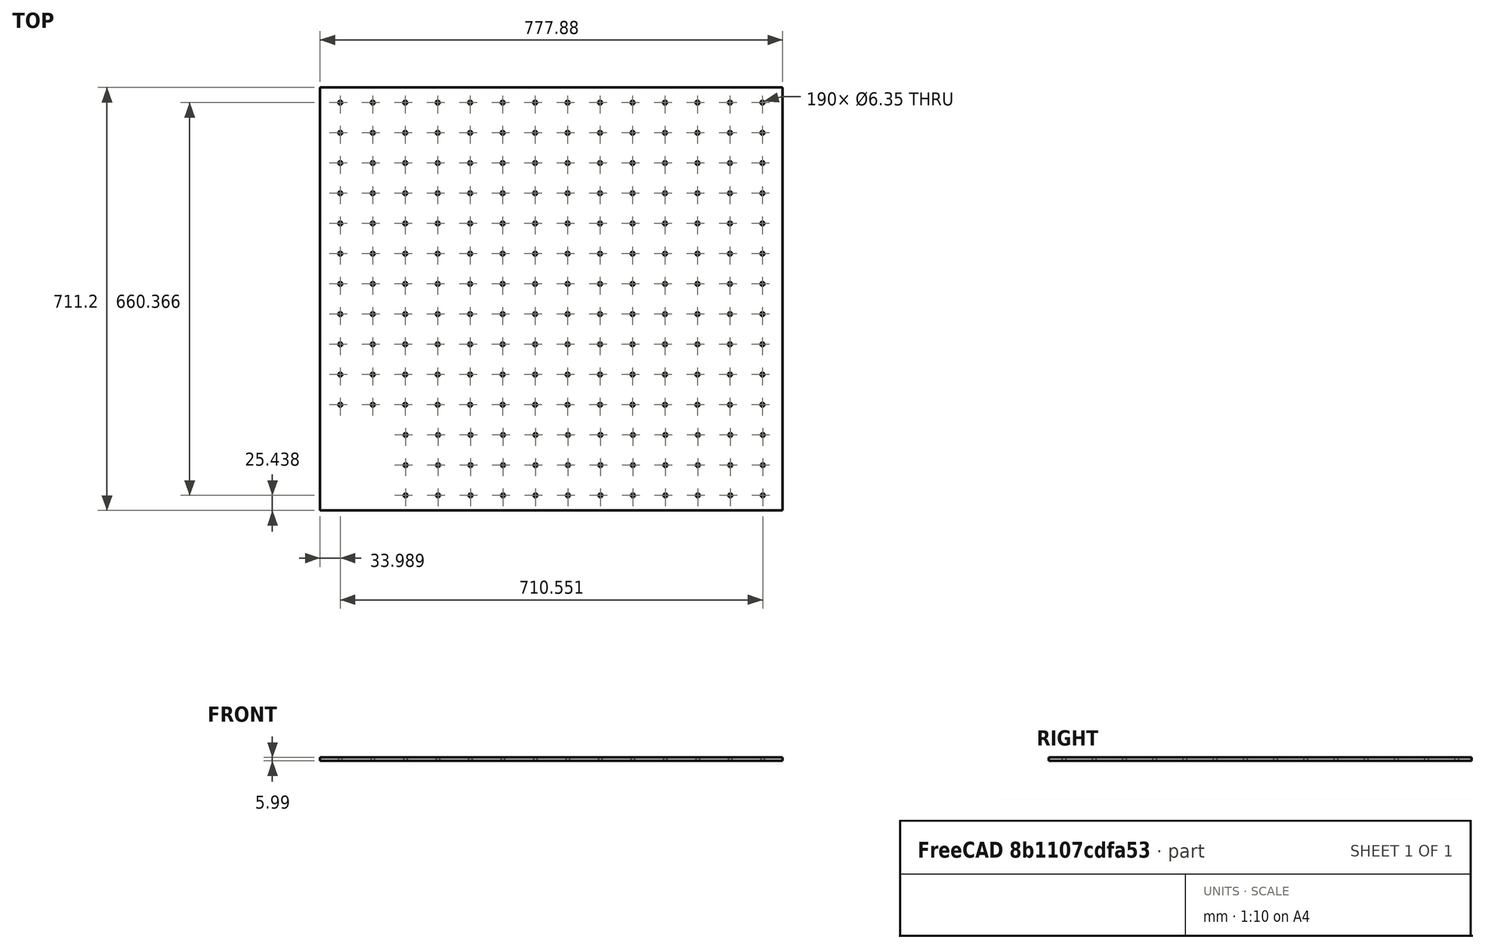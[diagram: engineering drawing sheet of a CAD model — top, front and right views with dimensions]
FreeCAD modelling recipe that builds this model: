
FCSTD DOCUMENT  (FreeCAD 0.19R24267 (Git))
Label: Inv1-P1
License: All rights reserved
LicenseURL: http://en.wikipedia.org/wiki/All_rights_reserved
objects: TechDraw::DrawViewDimension×8, TechDraw::DrawViewAnnotation×3, TechDraw::DrawProjGroupItem×2, TechDraw::DrawHatch×2, Sketcher::SketchObject×1, Part::Extrusion×1, TechDraw::DrawSVGTemplate×1, TechDraw::DrawProjGroup×1, TechDraw::DrawPage×1
note: 2 computed .brp shape members not serialized (recipe doc carries the construction recipe); baked Part::Feature solids carry a one-line shape summary decoded from their .brp

FEATURE [Sketcher::SketchObject] Sketch
  FullyConstrained = false
  sketch-geometry (389):
    g0: LineSegment StartX=-440.566 StartY=477.933 StartZ=0 EndX=337.309 EndY=477.933 EndZ=0
    g1: LineSegment StartX=337.309 StartY=477.933 StartZ=0 EndX=337.309 EndY=-233.267 EndZ=0
    g2: LineSegment StartX=337.309 StartY=-233.267 StartZ=0 EndX=-440.566 EndY=-233.267 EndZ=0
    g3: LineSegment StartX=-440.566 StartY=-233.267 StartZ=0 EndX=-440.566 EndY=477.933 EndZ=0
    g4: Circle CenterX=-406.581 CenterY=452.533 CenterZ=0 NormalX=0 NormalY=0 NormalZ=1 AngleXU=0 Radius=3.175
    g5: Circle CenterX=-351.971 CenterY=452.533 CenterZ=0 NormalX=0 NormalY=0 NormalZ=1 AngleXU=0 Radius=3.175
    g6: LineSegment StartX=-406.581 StartY=452.533 StartZ=0 EndX=-351.971 EndY=452.533 EndZ=0
    g7: Circle CenterX=-297.361 CenterY=452.533 CenterZ=0 NormalX=0 NormalY=0 NormalZ=1 AngleXU=0 Radius=3.175
    g8: LineSegment StartX=-351.971 StartY=452.533 StartZ=0 EndX=-297.361 EndY=452.533 EndZ=0
    g9: Circle CenterX=-242.751 CenterY=452.533 CenterZ=0 NormalX=0 NormalY=0 NormalZ=1 AngleXU=0 Radius=3.175
    g10: LineSegment StartX=-297.361 StartY=452.533 StartZ=0 EndX=-242.751 EndY=452.533 EndZ=0
    g11: Circle CenterX=-188.141 CenterY=452.533 CenterZ=0 NormalX=0 NormalY=0 NormalZ=1 AngleXU=0 Radius=3.175
    g12: LineSegment StartX=-242.751 StartY=452.533 StartZ=0 EndX=-188.141 EndY=452.533 EndZ=0
    g13: Circle CenterX=-133.531 CenterY=452.533 CenterZ=0 NormalX=0 NormalY=0 NormalZ=1 AngleXU=0 Radius=3.175
    g14: LineSegment StartX=-188.141 StartY=452.533 StartZ=0 EndX=-133.531 EndY=452.533 EndZ=0
    g15: Circle CenterX=-78.9213 CenterY=452.533 CenterZ=0 NormalX=0 NormalY=0 NormalZ=1 AngleXU=0 Radius=3.175
    g16: LineSegment StartX=-133.531 StartY=452.533 StartZ=0 EndX=-78.9213 EndY=452.533 EndZ=0
    g17: Circle CenterX=-24.3113 CenterY=452.533 CenterZ=0 NormalX=0 NormalY=0 NormalZ=1 AngleXU=0 Radius=3.175
    g18: LineSegment StartX=-78.9213 StartY=452.533 StartZ=0 EndX=-24.3113 EndY=452.533 EndZ=0
    g19: Circle CenterX=30.2987 CenterY=452.533 CenterZ=0 NormalX=0 NormalY=0 NormalZ=1 AngleXU=0 Radius=3.175
    g20: LineSegment StartX=-24.3113 StartY=452.533 StartZ=0 EndX=30.2987 EndY=452.533 EndZ=0
    g21: Circle CenterX=84.9087 CenterY=452.533 CenterZ=0 NormalX=0 NormalY=0 NormalZ=1 AngleXU=0 Radius=3.175
    g22: LineSegment StartX=30.2987 StartY=452.533 StartZ=0 EndX=84.9087 EndY=452.533 EndZ=0
    g23: Circle CenterX=139.519 CenterY=452.533 CenterZ=0 NormalX=0 NormalY=0 NormalZ=1 AngleXU=0 Radius=3.175
    g24: LineSegment StartX=84.9087 StartY=452.533 StartZ=0 EndX=139.519 EndY=452.533 EndZ=0
    g25: Circle CenterX=194.129 CenterY=452.533 CenterZ=0 NormalX=0 NormalY=0 NormalZ=1 AngleXU=0 Radius=3.175
    g26: LineSegment StartX=139.519 StartY=452.533 StartZ=0 EndX=194.129 EndY=452.533 EndZ=0
    g27: Circle CenterX=248.739 CenterY=452.533 CenterZ=0 NormalX=0 NormalY=0 NormalZ=1 AngleXU=0 Radius=3.175
    g28: LineSegment StartX=194.129 StartY=452.533 StartZ=0 EndX=248.739 EndY=452.533 EndZ=0
    g29: Circle CenterX=303.349 CenterY=452.533 CenterZ=0 NormalX=0 NormalY=0 NormalZ=1 AngleXU=0 Radius=3.175
    g30: LineSegment StartX=248.739 StartY=452.533 StartZ=0 EndX=303.349 EndY=452.533 EndZ=0
    g31: Circle CenterX=-406.581 CenterY=401.733 CenterZ=0 NormalX=0 NormalY=0 NormalZ=1 AngleXU=0 Radius=3.175
    g32: LineSegment StartX=-406.581 StartY=452.533 StartZ=0 EndX=-406.581 EndY=401.733 EndZ=0
    g33: Circle CenterX=-351.971 CenterY=401.733 CenterZ=0 NormalX=0 NormalY=0 NormalZ=1 AngleXU=0 Radius=3.175
    g34: LineSegment StartX=-406.581 StartY=401.733 StartZ=0 EndX=-351.971 EndY=401.733 EndZ=0
    g35: Circle CenterX=-297.361 CenterY=401.733 CenterZ=0 NormalX=0 NormalY=0 NormalZ=1 AngleXU=0 Radius=3.175
    g36: LineSegment StartX=-351.971 StartY=401.733 StartZ=0 EndX=-297.361 EndY=401.733 EndZ=0
    g37: Circle CenterX=-242.751 CenterY=401.733 CenterZ=0 NormalX=0 NormalY=0 NormalZ=1 AngleXU=0 Radius=3.175
    g38: LineSegment StartX=-297.361 StartY=401.733 StartZ=0 EndX=-242.751 EndY=401.733 EndZ=0
    g39: Circle CenterX=-188.141 CenterY=401.733 CenterZ=0 NormalX=0 NormalY=0 NormalZ=1 AngleXU=0 Radius=3.175
    g40: LineSegment StartX=-242.751 StartY=401.733 StartZ=0 EndX=-188.141 EndY=401.733 EndZ=0
    g41: Circle CenterX=-133.531 CenterY=401.733 CenterZ=0 NormalX=0 NormalY=0 NormalZ=1 AngleXU=0 Radius=3.175
    g42: LineSegment StartX=-188.141 StartY=401.733 StartZ=0 EndX=-133.531 EndY=401.733 EndZ=0
    g43: Circle CenterX=-78.9213 CenterY=401.733 CenterZ=0 NormalX=0 NormalY=0 NormalZ=1 AngleXU=0 Radius=3.175
    g44: LineSegment StartX=-133.531 StartY=401.733 StartZ=0 EndX=-78.9213 EndY=401.733 EndZ=0
    g45: Circle CenterX=-24.3113 CenterY=401.733 CenterZ=0 NormalX=0 NormalY=0 NormalZ=1 AngleXU=0 Radius=3.175
    g46: LineSegment StartX=-78.9213 StartY=401.733 StartZ=0 EndX=-24.3113 EndY=401.733 EndZ=0
    g47: Circle CenterX=30.2987 CenterY=401.733 CenterZ=0 NormalX=0 NormalY=0 NormalZ=1 AngleXU=0 Radius=3.175
    g48: LineSegment StartX=-24.3113 StartY=401.733 StartZ=0 EndX=30.2987 EndY=401.733 EndZ=0
    g49: Circle CenterX=84.9087 CenterY=401.733 CenterZ=0 NormalX=0 NormalY=0 NormalZ=1 AngleXU=0 Radius=3.175
    g50: LineSegment StartX=30.2987 StartY=401.733 StartZ=0 EndX=84.9087 EndY=401.733 EndZ=0
    g51: Circle CenterX=139.519 CenterY=401.733 CenterZ=0 NormalX=0 NormalY=0 NormalZ=1 AngleXU=0 Radius=3.175
    g52: LineSegment StartX=84.9087 StartY=401.733 StartZ=0 EndX=139.519 EndY=401.733 EndZ=0
    g53: Circle CenterX=194.129 CenterY=401.733 CenterZ=0 NormalX=0 NormalY=0 NormalZ=1 AngleXU=0 Radius=3.175
    g54: LineSegment StartX=139.519 StartY=401.733 StartZ=0 EndX=194.129 EndY=401.733 EndZ=0
    g55: Circle CenterX=248.739 CenterY=401.733 CenterZ=0 NormalX=0 NormalY=0 NormalZ=1 AngleXU=0 Radius=3.175
    g56: LineSegment StartX=194.129 StartY=401.733 StartZ=0 EndX=248.739 EndY=401.733 EndZ=0
    g57: Circle CenterX=303.349 CenterY=401.733 CenterZ=0 NormalX=0 NormalY=0 NormalZ=1 AngleXU=0 Radius=3.175
    g58: LineSegment StartX=248.739 StartY=401.733 StartZ=0 EndX=303.349 EndY=401.733 EndZ=0
    g59: Circle CenterX=-406.581 CenterY=350.933 CenterZ=0 NormalX=0 NormalY=0 NormalZ=1 AngleXU=0 Radius=3.175
    g60: LineSegment StartX=-406.581 StartY=401.733 StartZ=0 EndX=-406.581 EndY=350.933 EndZ=0
    g61: Circle CenterX=-351.971 CenterY=350.933 CenterZ=0 NormalX=0 NormalY=0 NormalZ=1 AngleXU=0 Radius=3.175
    g62: LineSegment StartX=-406.581 StartY=350.933 StartZ=0 EndX=-351.971 EndY=350.933 EndZ=0
    g63: Circle CenterX=-297.361 CenterY=350.933 CenterZ=0 NormalX=0 NormalY=0 NormalZ=1 AngleXU=0 Radius=3.175
    g64: LineSegment StartX=-351.971 StartY=350.933 StartZ=0 EndX=-297.361 EndY=350.933 EndZ=0
    g65: Circle CenterX=-242.751 CenterY=350.933 CenterZ=0 NormalX=0 NormalY=0 NormalZ=1 AngleXU=0 Radius=3.175
    g66: LineSegment StartX=-297.361 StartY=350.933 StartZ=0 EndX=-242.751 EndY=350.933 EndZ=0
    g67: Circle CenterX=-188.141 CenterY=350.933 CenterZ=0 NormalX=0 NormalY=0 NormalZ=1 AngleXU=0 Radius=3.175
    g68: LineSegment StartX=-242.751 StartY=350.933 StartZ=0 EndX=-188.141 EndY=350.933 EndZ=0
    g69: Circle CenterX=-133.531 CenterY=350.933 CenterZ=0 NormalX=0 NormalY=0 NormalZ=1 AngleXU=0 Radius=3.175
    g70: LineSegment StartX=-188.141 StartY=350.933 StartZ=0 EndX=-133.531 EndY=350.933 EndZ=0
    g71: Circle CenterX=-78.9213 CenterY=350.933 CenterZ=0 NormalX=0 NormalY=0 NormalZ=1 AngleXU=0 Radius=3.175
    g72: LineSegment StartX=-133.531 StartY=350.933 StartZ=0 EndX=-78.9213 EndY=350.933 EndZ=0
    g73: Circle CenterX=-24.3113 CenterY=350.933 CenterZ=0 NormalX=0 NormalY=0 NormalZ=1 AngleXU=0 Radius=3.175
    g74: LineSegment StartX=-78.9213 StartY=350.933 StartZ=0 EndX=-24.3113 EndY=350.933 EndZ=0
    g75: Circle CenterX=30.2987 CenterY=350.933 CenterZ=0 NormalX=0 NormalY=0 NormalZ=1 AngleXU=0 Radius=3.175
    g76: LineSegment StartX=-24.3113 StartY=350.933 StartZ=0 EndX=30.2987 EndY=350.933 EndZ=0
    g77: Circle CenterX=84.9087 CenterY=350.933 CenterZ=0 NormalX=0 NormalY=0 NormalZ=1 AngleXU=0 Radius=3.175
    g78: LineSegment StartX=30.2987 StartY=350.933 StartZ=0 EndX=84.9087 EndY=350.933 EndZ=0
    g79: Circle CenterX=139.519 CenterY=350.933 CenterZ=0 NormalX=0 NormalY=0 NormalZ=1 AngleXU=0 Radius=3.175
    g80: LineSegment StartX=84.9087 StartY=350.933 StartZ=0 EndX=139.519 EndY=350.933 EndZ=0
    g81: Circle CenterX=194.129 CenterY=350.933 CenterZ=0 NormalX=0 NormalY=0 NormalZ=1 AngleXU=0 Radius=3.175
    g82: LineSegment StartX=139.519 StartY=350.933 StartZ=0 EndX=194.129 EndY=350.933 EndZ=0
    g83: Circle CenterX=248.739 CenterY=350.933 CenterZ=0 NormalX=0 NormalY=0 NormalZ=1 AngleXU=0 Radius=3.175
    g84: LineSegment StartX=194.129 StartY=350.933 StartZ=0 EndX=248.739 EndY=350.933 EndZ=0
    g85: Circle CenterX=303.349 CenterY=350.933 CenterZ=0 NormalX=0 NormalY=0 NormalZ=1 AngleXU=0 Radius=3.175
    g86: LineSegment StartX=248.739 StartY=350.933 StartZ=0 EndX=303.349 EndY=350.933 EndZ=0
    g87: Circle CenterX=-406.581 CenterY=300.133 CenterZ=0 NormalX=0 NormalY=0 NormalZ=1 AngleXU=0 Radius=3.175
    g88: LineSegment StartX=-406.581 StartY=350.933 StartZ=0 EndX=-406.581 EndY=300.133 EndZ=0
    g89: Circle CenterX=-351.971 CenterY=300.133 CenterZ=0 NormalX=0 NormalY=0 NormalZ=1 AngleXU=0 Radius=3.175
    g90: LineSegment StartX=-406.581 StartY=300.133 StartZ=0 EndX=-351.971 EndY=300.133 EndZ=0
    g91: Circle CenterX=-297.361 CenterY=300.133 CenterZ=0 NormalX=0 NormalY=0 NormalZ=1 AngleXU=0 Radius=3.175
    g92: LineSegment StartX=-351.971 StartY=300.133 StartZ=0 EndX=-297.361 EndY=300.133 EndZ=0
    g93: Circle CenterX=-242.751 CenterY=300.133 CenterZ=0 NormalX=0 NormalY=0 NormalZ=1 AngleXU=0 Radius=3.175
    g94: LineSegment StartX=-297.361 StartY=300.133 StartZ=0 EndX=-242.751 EndY=300.133 EndZ=0
    g95: Circle CenterX=-188.141 CenterY=300.133 CenterZ=0 NormalX=0 NormalY=0 NormalZ=1 AngleXU=0 Radius=3.175
    g96: LineSegment StartX=-242.751 StartY=300.133 StartZ=0 EndX=-188.141 EndY=300.133 EndZ=0
    g97: Circle CenterX=-133.531 CenterY=300.133 CenterZ=0 NormalX=0 NormalY=0 NormalZ=1 AngleXU=0 Radius=3.175
    g98: LineSegment StartX=-188.141 StartY=300.133 StartZ=0 EndX=-133.531 EndY=300.133 EndZ=0
    g99: Circle CenterX=-78.9213 CenterY=300.133 CenterZ=0 NormalX=0 NormalY=0 NormalZ=1 AngleXU=0 Radius=3.175
    g100: LineSegment StartX=-133.531 StartY=300.133 StartZ=0 EndX=-78.9213 EndY=300.133 EndZ=0
    g101: Circle CenterX=-24.3113 CenterY=300.133 CenterZ=0 NormalX=0 NormalY=0 NormalZ=1 AngleXU=0 Radius=3.175
    g102: LineSegment StartX=-78.9213 StartY=300.133 StartZ=0 EndX=-24.3113 EndY=300.133 EndZ=0
    g103: Circle CenterX=30.2987 CenterY=300.133 CenterZ=0 NormalX=0 NormalY=0 NormalZ=1 AngleXU=0 Radius=3.175
    g104: LineSegment StartX=-24.3113 StartY=300.133 StartZ=0 EndX=30.2987 EndY=300.133 EndZ=0
    g105: Circle CenterX=84.9087 CenterY=300.133 CenterZ=0 NormalX=0 NormalY=0 NormalZ=1 AngleXU=0 Radius=3.175
    g106: LineSegment StartX=30.2987 StartY=300.133 StartZ=0 EndX=84.9087 EndY=300.133 EndZ=0
    g107: Circle CenterX=139.519 CenterY=300.133 CenterZ=0 NormalX=0 NormalY=0 NormalZ=1 AngleXU=0 Radius=3.175
    g108: LineSegment StartX=84.9087 StartY=300.133 StartZ=0 EndX=139.519 EndY=300.133 EndZ=0
    g109: Circle CenterX=194.129 CenterY=300.133 CenterZ=0 NormalX=0 NormalY=0 NormalZ=1 AngleXU=0 Radius=3.175
    g110: LineSegment StartX=139.519 StartY=300.133 StartZ=0 EndX=194.129 EndY=300.133 EndZ=0
    g111: Circle CenterX=248.739 CenterY=300.133 CenterZ=0 NormalX=0 NormalY=0 NormalZ=1 AngleXU=0 Radius=3.175
    g112: LineSegment StartX=194.129 StartY=300.133 StartZ=0 EndX=248.739 EndY=300.133 EndZ=0
    g113: Circle CenterX=303.349 CenterY=300.133 CenterZ=0 NormalX=0 NormalY=0 NormalZ=1 AngleXU=0 Radius=3.175
    g114: LineSegment StartX=248.739 StartY=300.133 StartZ=0 EndX=303.349 EndY=300.133 EndZ=0
    g115: Circle CenterX=-406.581 CenterY=249.333 CenterZ=0 NormalX=0 NormalY=0 NormalZ=1 AngleXU=0 Radius=3.175
    g116: LineSegment StartX=-406.581 StartY=300.133 StartZ=0 EndX=-406.581 EndY=249.333 EndZ=0
    g117: Circle CenterX=-351.971 CenterY=249.333 CenterZ=0 NormalX=0 NormalY=0 NormalZ=1 AngleXU=0 Radius=3.175
    g118: LineSegment StartX=-406.581 StartY=249.333 StartZ=0 EndX=-351.971 EndY=249.333 EndZ=0
    g119: Circle CenterX=-297.361 CenterY=249.333 CenterZ=0 NormalX=0 NormalY=0 NormalZ=1 AngleXU=0 Radius=3.175
    g120: LineSegment StartX=-351.971 StartY=249.333 StartZ=0 EndX=-297.361 EndY=249.333 EndZ=0
    g121: Circle CenterX=-242.751 CenterY=249.333 CenterZ=0 NormalX=0 NormalY=0 NormalZ=1 AngleXU=0 Radius=3.175
    g122: LineSegment StartX=-297.361 StartY=249.333 StartZ=0 EndX=-242.751 EndY=249.333 EndZ=0
    g123: Circle CenterX=-188.141 CenterY=249.333 CenterZ=0 NormalX=0 NormalY=0 NormalZ=1 AngleXU=0 Radius=3.175
    g124: LineSegment StartX=-242.751 StartY=249.333 StartZ=0 EndX=-188.141 EndY=249.333 EndZ=0
    g125: Circle CenterX=-133.531 CenterY=249.333 CenterZ=0 NormalX=0 NormalY=0 NormalZ=1 AngleXU=0 Radius=3.175
    g126: LineSegment StartX=-188.141 StartY=249.333 StartZ=0 EndX=-133.531 EndY=249.333 EndZ=0
    g127: Circle CenterX=-78.9213 CenterY=249.333 CenterZ=0 NormalX=0 NormalY=0 NormalZ=1 AngleXU=0 Radius=3.175
    g128: LineSegment StartX=-133.531 StartY=249.333 StartZ=0 EndX=-78.9213 EndY=249.333 EndZ=0
    g129: Circle CenterX=-24.3113 CenterY=249.333 CenterZ=0 NormalX=0 NormalY=0 NormalZ=1 AngleXU=0 Radius=3.175
    g130: LineSegment StartX=-78.9213 StartY=249.333 StartZ=0 EndX=-24.3113 EndY=249.333 EndZ=0
    g131: Circle CenterX=30.2987 CenterY=249.333 CenterZ=0 NormalX=0 NormalY=0 NormalZ=1 AngleXU=0 Radius=3.175
    g132: LineSegment StartX=-24.3113 StartY=249.333 StartZ=0 EndX=30.2987 EndY=249.333 EndZ=0
    g133: Circle CenterX=84.9087 CenterY=249.333 CenterZ=0 NormalX=0 NormalY=0 NormalZ=1 AngleXU=0 Radius=3.175
    g134: LineSegment StartX=30.2987 StartY=249.333 StartZ=0 EndX=84.9087 EndY=249.333 EndZ=0
    g135: Circle CenterX=139.519 CenterY=249.333 CenterZ=0 NormalX=0 NormalY=0 NormalZ=1 AngleXU=0 Radius=3.175
    g136: LineSegment StartX=84.9087 StartY=249.333 StartZ=0 EndX=139.519 EndY=249.333 EndZ=0
    g137: Circle CenterX=194.129 CenterY=249.333 CenterZ=0 NormalX=0 NormalY=0 NormalZ=1 AngleXU=0 Radius=3.175
    g138: LineSegment StartX=139.519 StartY=249.333 StartZ=0 EndX=194.129 EndY=249.333 EndZ=0
    g139: Circle CenterX=248.739 CenterY=249.333 CenterZ=0 NormalX=0 NormalY=0 NormalZ=1 AngleXU=0 Radius=3.175
    g140: LineSegment StartX=194.129 StartY=249.333 StartZ=0 EndX=248.739 EndY=249.333 EndZ=0
    g141: Circle CenterX=303.349 CenterY=249.333 CenterZ=0 NormalX=0 NormalY=0 NormalZ=1 AngleXU=0 Radius=3.175
    g142: LineSegment StartX=248.739 StartY=249.333 StartZ=0 EndX=303.349 EndY=249.333 EndZ=0
    g143: Circle CenterX=-406.581 CenterY=198.533 CenterZ=0 NormalX=0 NormalY=0 NormalZ=1 AngleXU=0 Radius=3.175
    g144: LineSegment StartX=-406.581 StartY=249.333 StartZ=0 EndX=-406.581 EndY=198.533 EndZ=0
    g145: Circle CenterX=-351.971 CenterY=198.533 CenterZ=0 NormalX=0 NormalY=0 NormalZ=1 AngleXU=0 Radius=3.175
    g146: LineSegment StartX=-406.581 StartY=198.533 StartZ=0 EndX=-351.971 EndY=198.533 EndZ=0
    g147: Circle CenterX=-297.361 CenterY=198.533 CenterZ=0 NormalX=0 NormalY=0 NormalZ=1 AngleXU=0 Radius=3.175
    g148: LineSegment StartX=-351.971 StartY=198.533 StartZ=0 EndX=-297.361 EndY=198.533 EndZ=0
    g149: Circle CenterX=-242.751 CenterY=198.533 CenterZ=0 NormalX=0 NormalY=0 NormalZ=1 AngleXU=0 Radius=3.175
    g150: LineSegment StartX=-297.361 StartY=198.533 StartZ=0 EndX=-242.751 EndY=198.533 EndZ=0
    g151: Circle CenterX=-188.141 CenterY=198.533 CenterZ=0 NormalX=0 NormalY=0 NormalZ=1 AngleXU=0 Radius=3.175
    g152: LineSegment StartX=-242.751 StartY=198.533 StartZ=0 EndX=-188.141 EndY=198.533 EndZ=0
    g153: Circle CenterX=-133.531 CenterY=198.533 CenterZ=0 NormalX=0 NormalY=0 NormalZ=1 AngleXU=0 Radius=3.175
    g154: LineSegment StartX=-188.141 StartY=198.533 StartZ=0 EndX=-133.531 EndY=198.533 EndZ=0
    g155: Circle CenterX=-78.9213 CenterY=198.533 CenterZ=0 NormalX=0 NormalY=0 NormalZ=1 AngleXU=0 Radius=3.175
    g156: LineSegment StartX=-133.531 StartY=198.533 StartZ=0 EndX=-78.9213 EndY=198.533 EndZ=0
    g157: Circle CenterX=-24.3113 CenterY=198.533 CenterZ=0 NormalX=0 NormalY=0 NormalZ=1 AngleXU=0 Radius=3.175
    g158: LineSegment StartX=-78.9213 StartY=198.533 StartZ=0 EndX=-24.3113 EndY=198.533 EndZ=0
    g159: Circle CenterX=30.2987 CenterY=198.533 CenterZ=0 NormalX=0 NormalY=0 NormalZ=1 AngleXU=0 Radius=3.175
    g160: LineSegment StartX=-24.3113 StartY=198.533 StartZ=0 EndX=30.2987 EndY=198.533 EndZ=0
    g161: Circle CenterX=84.9087 CenterY=198.533 CenterZ=0 NormalX=0 NormalY=0 NormalZ=1 AngleXU=0 Radius=3.175
    g162: LineSegment StartX=30.2987 StartY=198.533 StartZ=0 EndX=84.9087 EndY=198.533 EndZ=0
    g163: Circle CenterX=139.519 CenterY=198.533 CenterZ=0 NormalX=0 NormalY=0 NormalZ=1 AngleXU=0 Radius=3.175
    g164: LineSegment StartX=84.9087 StartY=198.533 StartZ=0 EndX=139.519 EndY=198.533 EndZ=0
    g165: Circle CenterX=194.129 CenterY=198.533 CenterZ=0 NormalX=0 NormalY=0 NormalZ=1 AngleXU=0 Radius=3.175
    g166: LineSegment StartX=139.519 StartY=198.533 StartZ=0 EndX=194.129 EndY=198.533 EndZ=0
    g167: Circle CenterX=248.739 CenterY=198.533 CenterZ=0 NormalX=0 NormalY=0 NormalZ=1 AngleXU=0 Radius=3.175
    g168: LineSegment StartX=194.129 StartY=198.533 StartZ=0 EndX=248.739 EndY=198.533 EndZ=0
    g169: Circle CenterX=303.349 CenterY=198.533 CenterZ=0 NormalX=0 NormalY=0 NormalZ=1 AngleXU=0 Radius=3.175
    g170: LineSegment StartX=248.739 StartY=198.533 StartZ=0 EndX=303.349 EndY=198.533 EndZ=0
    g171: Circle CenterX=-406.581 CenterY=147.733 CenterZ=0 NormalX=0 NormalY=0 NormalZ=1 AngleXU=0 Radius=3.175
    g172: LineSegment StartX=-406.581 StartY=198.533 StartZ=0 EndX=-406.581 EndY=147.733 EndZ=0
    g173: Circle CenterX=-351.971 CenterY=147.733 CenterZ=0 NormalX=0 NormalY=0 NormalZ=1 AngleXU=0 Radius=3.175
    g174: LineSegment StartX=-406.581 StartY=147.733 StartZ=0 EndX=-351.971 EndY=147.733 EndZ=0
    g175: Circle CenterX=-297.361 CenterY=147.733 CenterZ=0 NormalX=0 NormalY=0 NormalZ=1 AngleXU=0 Radius=3.175
    g176: LineSegment StartX=-351.971 StartY=147.733 StartZ=0 EndX=-297.361 EndY=147.733 EndZ=0
    g177: Circle CenterX=-242.751 CenterY=147.733 CenterZ=0 NormalX=0 NormalY=0 NormalZ=1 AngleXU=0 Radius=3.175
    g178: LineSegment StartX=-297.361 StartY=147.733 StartZ=0 EndX=-242.751 EndY=147.733 EndZ=0
    g179: Circle CenterX=-188.141 CenterY=147.733 CenterZ=0 NormalX=0 NormalY=0 NormalZ=1 AngleXU=0 Radius=3.175
    g180: LineSegment StartX=-242.751 StartY=147.733 StartZ=0 EndX=-188.141 EndY=147.733 EndZ=0
    g181: Circle CenterX=-133.531 CenterY=147.733 CenterZ=0 NormalX=0 NormalY=0 NormalZ=1 AngleXU=0 Radius=3.175
    g182: LineSegment StartX=-188.141 StartY=147.733 StartZ=0 EndX=-133.531 EndY=147.733 EndZ=0
    g183: Circle CenterX=-78.9213 CenterY=147.733 CenterZ=0 NormalX=0 NormalY=0 NormalZ=1 AngleXU=0 Radius=3.175
    g184: LineSegment StartX=-133.531 StartY=147.733 StartZ=0 EndX=-78.9213 EndY=147.733 EndZ=0
    g185: Circle CenterX=-24.3113 CenterY=147.733 CenterZ=0 NormalX=0 NormalY=0 NormalZ=1 AngleXU=0 Radius=3.175
    g186: LineSegment StartX=-78.9213 StartY=147.733 StartZ=0 EndX=-24.3113 EndY=147.733 EndZ=0
    g187: Circle CenterX=30.2987 CenterY=147.733 CenterZ=0 NormalX=0 NormalY=0 NormalZ=1 AngleXU=0 Radius=3.175
    g188: LineSegment StartX=-24.3113 StartY=147.733 StartZ=0 EndX=30.2987 EndY=147.733 EndZ=0
    g189: Circle CenterX=84.9087 CenterY=147.733 CenterZ=0 NormalX=0 NormalY=0 NormalZ=1 AngleXU=0 Radius=3.175
    g190: LineSegment StartX=30.2987 StartY=147.733 StartZ=0 EndX=84.9087 EndY=147.733 EndZ=0
    g191: Circle CenterX=139.519 CenterY=147.733 CenterZ=0 NormalX=0 NormalY=0 NormalZ=1 AngleXU=0 Radius=3.175
    g192: LineSegment StartX=84.9087 StartY=147.733 StartZ=0 EndX=139.519 EndY=147.733 EndZ=0
    g193: Circle CenterX=194.129 CenterY=147.733 CenterZ=0 NormalX=0 NormalY=0 NormalZ=1 AngleXU=0 Radius=3.175
    g194: LineSegment StartX=139.519 StartY=147.733 StartZ=0 EndX=194.129 EndY=147.733 EndZ=0
    g195: Circle CenterX=248.739 CenterY=147.733 CenterZ=0 NormalX=0 NormalY=0 NormalZ=1 AngleXU=0 Radius=3.175
    g196: LineSegment StartX=194.129 StartY=147.733 StartZ=0 EndX=248.739 EndY=147.733 EndZ=0
    g197: Circle CenterX=303.349 CenterY=147.733 CenterZ=0 NormalX=0 NormalY=0 NormalZ=1 AngleXU=0 Radius=3.175
    g198: LineSegment StartX=248.739 StartY=147.733 StartZ=0 EndX=303.349 EndY=147.733 EndZ=0
    g199: Circle CenterX=-406.581 CenterY=96.9335 CenterZ=0 NormalX=0 NormalY=0 NormalZ=1 AngleXU=0 Radius=3.175
    g200: LineSegment StartX=-406.581 StartY=147.733 StartZ=0 EndX=-406.581 EndY=96.9335 EndZ=0
    g201: Circle CenterX=-351.971 CenterY=96.9335 CenterZ=0 NormalX=0 NormalY=0 NormalZ=1 AngleXU=0 Radius=3.175
    g202: LineSegment StartX=-406.581 StartY=96.9335 StartZ=0 EndX=-351.971 EndY=96.9335 EndZ=0
    g203: Circle CenterX=-297.361 CenterY=96.9335 CenterZ=0 NormalX=0 NormalY=0 NormalZ=1 AngleXU=0 Radius=3.175
    g204: LineSegment StartX=-351.971 StartY=96.9335 StartZ=0 EndX=-297.361 EndY=96.9335 EndZ=0
    g205: Circle CenterX=-242.751 CenterY=96.9335 CenterZ=0 NormalX=0 NormalY=0 NormalZ=1 AngleXU=0 Radius=3.175
    g206: LineSegment StartX=-297.361 StartY=96.9335 StartZ=0 EndX=-242.751 EndY=96.9335 EndZ=0
    g207: Circle CenterX=-188.141 CenterY=96.9335 CenterZ=0 NormalX=0 NormalY=0 NormalZ=1 AngleXU=0 Radius=3.175
    g208: LineSegment StartX=-242.751 StartY=96.9335 StartZ=0 EndX=-188.141 EndY=96.9335 EndZ=0
    g209: Circle CenterX=-133.531 CenterY=96.9335 CenterZ=0 NormalX=0 NormalY=0 NormalZ=1 AngleXU=0 Radius=3.175
    g210: LineSegment StartX=-188.141 StartY=96.9335 StartZ=0 EndX=-133.531 EndY=96.9335 EndZ=0
    g211: Circle CenterX=-78.9213 CenterY=96.9335 CenterZ=0 NormalX=0 NormalY=0 NormalZ=1 AngleXU=0 Radius=3.175
    g212: LineSegment StartX=-133.531 StartY=96.9335 StartZ=0 EndX=-78.9213 EndY=96.9335 EndZ=0
    g213: Circle CenterX=-24.3113 CenterY=96.9335 CenterZ=0 NormalX=0 NormalY=0 NormalZ=1 AngleXU=0 Radius=3.175
    g214: LineSegment StartX=-78.9213 StartY=96.9335 StartZ=0 EndX=-24.3113 EndY=96.9335 EndZ=0
    g215: Circle CenterX=30.2987 CenterY=96.9335 CenterZ=0 NormalX=0 NormalY=0 NormalZ=1 AngleXU=0 Radius=3.175
    g216: LineSegment StartX=-24.3113 StartY=96.9335 StartZ=0 EndX=30.2987 EndY=96.9335 EndZ=0
    g217: Circle CenterX=84.9087 CenterY=96.9335 CenterZ=0 NormalX=0 NormalY=0 NormalZ=1 AngleXU=0 Radius=3.175
    g218: LineSegment StartX=30.2987 StartY=96.9335 StartZ=0 EndX=84.9087 EndY=96.9335 EndZ=0
    g219: Circle CenterX=139.519 CenterY=96.9335 CenterZ=0 NormalX=0 NormalY=0 NormalZ=1 AngleXU=0 Radius=3.175
    g220: LineSegment StartX=84.9087 StartY=96.9335 StartZ=0 EndX=139.519 EndY=96.9335 EndZ=0
    g221: Circle CenterX=194.129 CenterY=96.9335 CenterZ=0 NormalX=0 NormalY=0 NormalZ=1 AngleXU=0 Radius=3.175
    g222: LineSegment StartX=139.519 StartY=96.9335 StartZ=0 EndX=194.129 EndY=96.9335 EndZ=0
    g223: Circle CenterX=248.739 CenterY=96.9335 CenterZ=0 NormalX=0 NormalY=0 NormalZ=1 AngleXU=0 Radius=3.175
    g224: LineSegment StartX=194.129 StartY=96.9335 StartZ=0 EndX=248.739 EndY=96.9335 EndZ=0
    g225: Circle CenterX=303.349 CenterY=96.9335 CenterZ=0 NormalX=0 NormalY=0 NormalZ=1 AngleXU=0 Radius=3.175
    g226: LineSegment StartX=248.739 StartY=96.9335 StartZ=0 EndX=303.349 EndY=96.9335 EndZ=0
    g227: Circle CenterX=-406.581 CenterY=46.1335 CenterZ=0 NormalX=0 NormalY=0 NormalZ=1 AngleXU=0 Radius=3.175
    g228: LineSegment StartX=-406.581 StartY=96.9335 StartZ=0 EndX=-406.581 EndY=46.1335 EndZ=0
    g229: Circle CenterX=-351.971 CenterY=46.1335 CenterZ=0 NormalX=0 NormalY=0 NormalZ=1 AngleXU=0 Radius=3.175
    g230: LineSegment StartX=-406.581 StartY=46.1335 StartZ=0 EndX=-351.971 EndY=46.1335 EndZ=0
    g231: Circle CenterX=-297.361 CenterY=46.1335 CenterZ=0 NormalX=0 NormalY=0 NormalZ=1 AngleXU=0 Radius=3.175
    g232: LineSegment StartX=-351.971 StartY=46.1335 StartZ=0 EndX=-297.361 EndY=46.1335 EndZ=0
    g233: Circle CenterX=-242.751 CenterY=46.1335 CenterZ=0 NormalX=0 NormalY=0 NormalZ=1 AngleXU=0 Radius=3.175
    g234: LineSegment StartX=-297.361 StartY=46.1335 StartZ=0 EndX=-242.751 EndY=46.1335 EndZ=0
    g235: Circle CenterX=-188.141 CenterY=46.1335 CenterZ=0 NormalX=0 NormalY=0 NormalZ=1 AngleXU=0 Radius=3.175
    g236: LineSegment StartX=-242.751 StartY=46.1335 StartZ=0 EndX=-188.141 EndY=46.1335 EndZ=0
    g237: Circle CenterX=-133.531 CenterY=46.1335 CenterZ=0 NormalX=0 NormalY=0 NormalZ=1 AngleXU=0 Radius=3.175
    g238: LineSegment StartX=-188.141 StartY=46.1335 StartZ=0 EndX=-133.531 EndY=46.1335 EndZ=0
    g239: Circle CenterX=-78.9213 CenterY=46.1335 CenterZ=0 NormalX=0 NormalY=0 NormalZ=1 AngleXU=0 Radius=3.175
    g240: LineSegment StartX=-133.531 StartY=46.1335 StartZ=0 EndX=-78.9213 EndY=46.1335 EndZ=0
    g241: Circle CenterX=-24.3113 CenterY=46.1335 CenterZ=0 NormalX=0 NormalY=0 NormalZ=1 AngleXU=0 Radius=3.175
    g242: LineSegment StartX=-78.9213 StartY=46.1335 StartZ=0 EndX=-24.3113 EndY=46.1335 EndZ=0
    g243: Circle CenterX=30.2987 CenterY=46.1335 CenterZ=0 NormalX=0 NormalY=0 NormalZ=1 AngleXU=0 Radius=3.175
    g244: LineSegment StartX=-24.3113 StartY=46.1335 StartZ=0 EndX=30.2987 EndY=46.1335 EndZ=0
    g245: Circle CenterX=84.9087 CenterY=46.1335 CenterZ=0 NormalX=0 NormalY=0 NormalZ=1 AngleXU=0 Radius=3.175
    g246: LineSegment StartX=30.2987 StartY=46.1335 StartZ=0 EndX=84.9087 EndY=46.1335 EndZ=0
    g247: Circle CenterX=139.519 CenterY=46.1335 CenterZ=0 NormalX=0 NormalY=0 NormalZ=1 AngleXU=0 Radius=3.175
    g248: LineSegment StartX=84.9087 StartY=46.1335 StartZ=0 EndX=139.519 EndY=46.1335 EndZ=0
    g249: Circle CenterX=194.129 CenterY=46.1335 CenterZ=0 NormalX=0 NormalY=0 NormalZ=1 AngleXU=0 Radius=3.175
    g250: LineSegment StartX=139.519 StartY=46.1335 StartZ=0 EndX=194.129 EndY=46.1335 EndZ=0
    g251: Circle CenterX=248.739 CenterY=46.1335 CenterZ=0 NormalX=0 NormalY=0 NormalZ=1 AngleXU=0 Radius=3.175
    g252: LineSegment StartX=194.129 StartY=46.1335 StartZ=0 EndX=248.739 EndY=46.1335 EndZ=0
    g253: Circle CenterX=303.349 CenterY=46.1335 CenterZ=0 NormalX=0 NormalY=0 NormalZ=1 AngleXU=0 Radius=3.175
    g254: LineSegment StartX=248.739 StartY=46.1335 StartZ=0 EndX=303.349 EndY=46.1335 EndZ=0
    g255: Circle CenterX=-406.581 CenterY=-4.66652 CenterZ=0 NormalX=0 NormalY=0 NormalZ=1 AngleXU=0 Radius=3.175
    g256: LineSegment StartX=-406.581 StartY=46.1335 StartZ=0 EndX=-406.581 EndY=-4.66652 EndZ=0
    g257: Circle CenterX=-351.971 CenterY=-4.66652 CenterZ=0 NormalX=0 NormalY=0 NormalZ=1 AngleXU=0 Radius=3.175
    g258: LineSegment StartX=-406.581 StartY=-4.66652 StartZ=0 EndX=-351.971 EndY=-4.66652 EndZ=0
    g259: Circle CenterX=-297.361 CenterY=-4.66652 CenterZ=0 NormalX=0 NormalY=0 NormalZ=1 AngleXU=0 Radius=3.175
    g260: LineSegment StartX=-351.971 StartY=-4.66652 StartZ=0 EndX=-297.361 EndY=-4.66652 EndZ=0
    g261: Circle CenterX=-242.751 CenterY=-4.66652 CenterZ=0 NormalX=0 NormalY=0 NormalZ=1 AngleXU=0 Radius=3.175
    g262: LineSegment StartX=-297.361 StartY=-4.66652 StartZ=0 EndX=-242.751 EndY=-4.66652 EndZ=0
    g263: Circle CenterX=-188.141 CenterY=-4.66652 CenterZ=0 NormalX=0 NormalY=0 NormalZ=1 AngleXU=0 Radius=3.175
    g264: LineSegment StartX=-242.751 StartY=-4.66652 StartZ=0 EndX=-188.141 EndY=-4.66652 EndZ=0
    g265: Circle CenterX=-133.531 CenterY=-4.66652 CenterZ=0 NormalX=0 NormalY=0 NormalZ=1 AngleXU=0 Radius=3.175
    g266: LineSegment StartX=-188.141 StartY=-4.66652 StartZ=0 EndX=-133.531 EndY=-4.66652 EndZ=0
    g267: Circle CenterX=-78.9213 CenterY=-4.66652 CenterZ=0 NormalX=0 NormalY=0 NormalZ=1 AngleXU=0 Radius=3.175
    g268: LineSegment StartX=-133.531 StartY=-4.66652 StartZ=0 EndX=-78.9213 EndY=-4.66652 EndZ=0
    g269: Circle CenterX=-24.3113 CenterY=-4.66652 CenterZ=0 NormalX=0 NormalY=0 NormalZ=1 AngleXU=0 Radius=3.175
    g270: LineSegment StartX=-78.9213 StartY=-4.66652 StartZ=0 EndX=-24.3113 EndY=-4.66652 EndZ=0
    g271: Circle CenterX=30.2987 CenterY=-4.66652 CenterZ=0 NormalX=0 NormalY=0 NormalZ=1 AngleXU=0 Radius=3.175
    g272: LineSegment StartX=-24.3113 StartY=-4.66652 StartZ=0 EndX=30.2987 EndY=-4.66652 EndZ=0
    g273: Circle CenterX=84.9087 CenterY=-4.66652 CenterZ=0 NormalX=0 NormalY=0 NormalZ=1 AngleXU=0 Radius=3.175
    g274: LineSegment StartX=30.2987 StartY=-4.66652 StartZ=0 EndX=84.9087 EndY=-4.66652 EndZ=0
    g275: Circle CenterX=139.519 CenterY=-4.66652 CenterZ=0 NormalX=0 NormalY=0 NormalZ=1 AngleXU=0 Radius=3.175
    g276: LineSegment StartX=84.9087 StartY=-4.66652 StartZ=0 EndX=139.519 EndY=-4.66652 EndZ=0
    g277: Circle CenterX=194.129 CenterY=-4.66652 CenterZ=0 NormalX=0 NormalY=0 NormalZ=1 AngleXU=0 Radius=3.175
    g278: LineSegment StartX=139.519 StartY=-4.66652 StartZ=0 EndX=194.129 EndY=-4.66652 EndZ=0
    g279: Circle CenterX=248.739 CenterY=-4.66652 CenterZ=0 NormalX=0 NormalY=0 NormalZ=1 AngleXU=0 Radius=3.175
    g280: LineSegment StartX=194.129 StartY=-4.66652 StartZ=0 EndX=248.739 EndY=-4.66652 EndZ=0
    g281: Circle CenterX=303.349 CenterY=-4.66652 CenterZ=0 NormalX=0 NormalY=0 NormalZ=1 AngleXU=0 Radius=3.175
    g282: LineSegment StartX=248.739 StartY=-4.66652 StartZ=0 EndX=303.349 EndY=-4.66652 EndZ=0
    g283: Circle CenterX=-406.581 CenterY=-55.4665 CenterZ=0 NormalX=0 NormalY=0 NormalZ=1 AngleXU=0 Radius=3.175
    g284: LineSegment StartX=-406.581 StartY=-4.66652 StartZ=0 EndX=-406.581 EndY=-55.4665 EndZ=0
    g285: Circle CenterX=-351.971 CenterY=-55.4665 CenterZ=0 NormalX=0 NormalY=0 NormalZ=1 AngleXU=0 Radius=3.175
    g286: LineSegment StartX=-406.581 StartY=-55.4665 StartZ=0 EndX=-351.971 EndY=-55.4665 EndZ=0
    g287: Circle CenterX=-297.361 CenterY=-55.4665 CenterZ=0 NormalX=0 NormalY=0 NormalZ=1 AngleXU=0 Radius=3.175
    g288: LineSegment StartX=-351.971 StartY=-55.4665 StartZ=0 EndX=-297.361 EndY=-55.4665 EndZ=0
    g289: Circle CenterX=-242.751 CenterY=-55.4665 CenterZ=0 NormalX=0 NormalY=0 NormalZ=1 AngleXU=0 Radius=3.175
    g290: LineSegment StartX=-297.361 StartY=-55.4665 StartZ=0 EndX=-242.751 EndY=-55.4665 EndZ=0
    g291: Circle CenterX=-188.141 CenterY=-55.4665 CenterZ=0 NormalX=0 NormalY=0 NormalZ=1 AngleXU=0 Radius=3.175
    g292: LineSegment StartX=-242.751 StartY=-55.4665 StartZ=0 EndX=-188.141 EndY=-55.4665 EndZ=0
    g293: Circle CenterX=-133.531 CenterY=-55.4665 CenterZ=0 NormalX=0 NormalY=0 NormalZ=1 AngleXU=0 Radius=3.175
    g294: LineSegment StartX=-188.141 StartY=-55.4665 StartZ=0 EndX=-133.531 EndY=-55.4665 EndZ=0
    g295: Circle CenterX=-78.9213 CenterY=-55.4665 CenterZ=0 NormalX=0 NormalY=0 NormalZ=1 AngleXU=0 Radius=3.175
    g296: LineSegment StartX=-133.531 StartY=-55.4665 StartZ=0 EndX=-78.9213 EndY=-55.4665 EndZ=0
    g297: Circle CenterX=-24.3113 CenterY=-55.4665 CenterZ=0 NormalX=0 NormalY=0 NormalZ=1 AngleXU=0 Radius=3.175
    g298: LineSegment StartX=-78.9213 StartY=-55.4665 StartZ=0 EndX=-24.3113 EndY=-55.4665 EndZ=0
    g299: Circle CenterX=30.2987 CenterY=-55.4665 CenterZ=0 NormalX=0 NormalY=0 NormalZ=1 AngleXU=0 Radius=3.175
    g300: LineSegment StartX=-24.3113 StartY=-55.4665 StartZ=0 EndX=30.2987 EndY=-55.4665 EndZ=0
    g301: Circle CenterX=84.9087 CenterY=-55.4665 CenterZ=0 NormalX=0 NormalY=0 NormalZ=1 AngleXU=0 Radius=3.175
    g302: LineSegment StartX=30.2987 StartY=-55.4665 StartZ=0 EndX=84.9087 EndY=-55.4665 EndZ=0
    g303: Circle CenterX=139.519 CenterY=-55.4665 CenterZ=0 NormalX=0 NormalY=0 NormalZ=1 AngleXU=0 Radius=3.175
    g304: LineSegment StartX=84.9087 StartY=-55.4665 StartZ=0 EndX=139.519 EndY=-55.4665 EndZ=0
    g305: Circle CenterX=194.129 CenterY=-55.4665 CenterZ=0 NormalX=0 NormalY=0 NormalZ=1 AngleXU=0 Radius=3.175
    g306: LineSegment StartX=139.519 StartY=-55.4665 StartZ=0 EndX=194.129 EndY=-55.4665 EndZ=0
    g307: Circle CenterX=248.739 CenterY=-55.4665 CenterZ=0 NormalX=0 NormalY=0 NormalZ=1 AngleXU=0 Radius=3.175
    g308: LineSegment StartX=194.129 StartY=-55.4665 StartZ=0 EndX=248.739 EndY=-55.4665 EndZ=0
    g309: Circle CenterX=303.349 CenterY=-55.4665 CenterZ=0 NormalX=0 NormalY=0 NormalZ=1 AngleXU=0 Radius=3.175
    g310: LineSegment StartX=248.739 StartY=-55.4665 StartZ=0 EndX=303.349 EndY=-55.4665 EndZ=0
    g311: LineSegment StartX=-406.581 StartY=-55.4665 StartZ=0 EndX=-406.581 EndY=-106.267 EndZ=0
    g312: LineSegment StartX=-405.96 StartY=-106.232 StartZ=0 EndX=-351.35 EndY=-106.232 EndZ=0
    g313: Circle CenterX=-296.741 CenterY=-106.232 CenterZ=0 NormalX=0 NormalY=0 NormalZ=1 AngleXU=0 Radius=3.175
    g314: LineSegment StartX=-351.351 StartY=-106.232 StartZ=0 EndX=-296.741 EndY=-106.232 EndZ=0
    g315: Circle CenterX=-242.131 CenterY=-106.232 CenterZ=0 NormalX=0 NormalY=0 NormalZ=1 AngleXU=0 Radius=3.175
    g316: LineSegment StartX=-296.741 StartY=-106.232 StartZ=0 EndX=-242.131 EndY=-106.232 EndZ=0
    g317: Circle CenterX=-187.521 CenterY=-106.232 CenterZ=0 NormalX=0 NormalY=0 NormalZ=1 AngleXU=0 Radius=3.175
    g318: LineSegment StartX=-242.131 StartY=-106.232 StartZ=0 EndX=-187.521 EndY=-106.232 EndZ=0
    g319: Circle CenterX=-132.911 CenterY=-106.232 CenterZ=0 NormalX=0 NormalY=0 NormalZ=1 AngleXU=0 Radius=3.175
    g320: LineSegment StartX=-187.521 StartY=-106.232 StartZ=0 EndX=-132.911 EndY=-106.232 EndZ=0
    g321: Circle CenterX=-78.3007 CenterY=-106.232 CenterZ=0 NormalX=0 NormalY=0 NormalZ=1 AngleXU=0 Radius=3.175
    g322: LineSegment StartX=-132.911 StartY=-106.232 StartZ=0 EndX=-78.3007 EndY=-106.232 EndZ=0
    g323: Circle CenterX=-23.6907 CenterY=-106.232 CenterZ=0 NormalX=0 NormalY=0 NormalZ=1 AngleXU=0 Radius=3.175
    g324: LineSegment StartX=-78.3007 StartY=-106.232 StartZ=0 EndX=-23.6907 EndY=-106.232 EndZ=0
    g325: Circle CenterX=30.9193 CenterY=-106.232 CenterZ=0 NormalX=0 NormalY=0 NormalZ=1 AngleXU=0 Radius=3.175
    g326: LineSegment StartX=-23.6907 StartY=-106.232 StartZ=0 EndX=30.9193 EndY=-106.232 EndZ=0
    g327: Circle CenterX=85.5293 CenterY=-106.232 CenterZ=0 NormalX=0 NormalY=0 NormalZ=1 AngleXU=0 Radius=3.175
    g328: LineSegment StartX=30.9193 StartY=-106.232 StartZ=0 EndX=85.5293 EndY=-106.232 EndZ=0
    g329: Circle CenterX=140.139 CenterY=-106.232 CenterZ=0 NormalX=0 NormalY=0 NormalZ=1 AngleXU=0 Radius=3.175
    g330: LineSegment StartX=85.5293 StartY=-106.232 StartZ=0 EndX=140.139 EndY=-106.232 EndZ=0
    g331: Circle CenterX=194.749 CenterY=-106.232 CenterZ=0 NormalX=0 NormalY=0 NormalZ=1 AngleXU=0 Radius=3.175
    g332: LineSegment StartX=140.139 StartY=-106.232 StartZ=0 EndX=194.749 EndY=-106.232 EndZ=0
    g333: Circle CenterX=249.359 CenterY=-106.232 CenterZ=0 NormalX=0 NormalY=0 NormalZ=1 AngleXU=0 Radius=3.175
    g334: LineSegment StartX=194.749 StartY=-106.232 StartZ=0 EndX=249.359 EndY=-106.232 EndZ=0
    g335: Circle CenterX=303.969 CenterY=-106.232 CenterZ=0 NormalX=0 NormalY=0 NormalZ=1 AngleXU=0 Radius=3.175
    g336: LineSegment StartX=249.359 StartY=-106.232 StartZ=0 EndX=303.969 EndY=-106.232 EndZ=0
    g337: LineSegment StartX=-405.961 StartY=-106.232 StartZ=0 EndX=-405.961 EndY=-157.032 EndZ=0
    g338: LineSegment StartX=-405.961 StartY=-157.032 StartZ=0 EndX=-351.351 EndY=-157.032 EndZ=0
    g339: Circle CenterX=-296.74 CenterY=-157.032 CenterZ=0 NormalX=0 NormalY=0 NormalZ=1 AngleXU=0 Radius=3.175
    g340: LineSegment StartX=-351.35 StartY=-157.032 StartZ=0 EndX=-296.74 EndY=-157.032 EndZ=0
    g341: Circle CenterX=-242.13 CenterY=-157.032 CenterZ=0 NormalX=0 NormalY=0 NormalZ=1 AngleXU=0 Radius=3.175
    g342: LineSegment StartX=-296.74 StartY=-157.032 StartZ=0 EndX=-242.13 EndY=-157.032 EndZ=0
    g343: Circle CenterX=-187.52 CenterY=-157.032 CenterZ=0 NormalX=0 NormalY=0 NormalZ=1 AngleXU=0 Radius=3.175
    g344: LineSegment StartX=-242.13 StartY=-157.032 StartZ=0 EndX=-187.52 EndY=-157.032 EndZ=0
    g345: Circle CenterX=-132.91 CenterY=-157.032 CenterZ=0 NormalX=0 NormalY=0 NormalZ=1 AngleXU=0 Radius=3.175
    g346: LineSegment StartX=-187.52 StartY=-157.032 StartZ=0 EndX=-132.91 EndY=-157.032 EndZ=0
    g347: Circle CenterX=-78.3004 CenterY=-157.032 CenterZ=0 NormalX=0 NormalY=0 NormalZ=1 AngleXU=0 Radius=3.175
    g348: LineSegment StartX=-132.91 StartY=-157.032 StartZ=0 EndX=-78.3004 EndY=-157.032 EndZ=0
    g349: Circle CenterX=-23.6904 CenterY=-157.032 CenterZ=0 NormalX=0 NormalY=0 NormalZ=1 AngleXU=0 Radius=3.175
    g350: LineSegment StartX=-78.3004 StartY=-157.032 StartZ=0 EndX=-23.6904 EndY=-157.032 EndZ=0
    g351: Circle CenterX=30.9196 CenterY=-157.032 CenterZ=0 NormalX=0 NormalY=0 NormalZ=1 AngleXU=0 Radius=3.175
    g352: LineSegment StartX=-23.6904 StartY=-157.032 StartZ=0 EndX=30.9196 EndY=-157.032 EndZ=0
    g353: Circle CenterX=85.5296 CenterY=-157.032 CenterZ=0 NormalX=0 NormalY=0 NormalZ=1 AngleXU=0 Radius=3.175
    g354: LineSegment StartX=30.9196 StartY=-157.032 StartZ=0 EndX=85.5296 EndY=-157.032 EndZ=0
    g355: Circle CenterX=140.14 CenterY=-157.032 CenterZ=0 NormalX=0 NormalY=0 NormalZ=1 AngleXU=0 Radius=3.175
    g356: LineSegment StartX=85.5296 StartY=-157.032 StartZ=0 EndX=140.14 EndY=-157.032 EndZ=0
    g357: Circle CenterX=194.75 CenterY=-157.032 CenterZ=0 NormalX=0 NormalY=0 NormalZ=1 AngleXU=0 Radius=3.175
    g358: LineSegment StartX=140.14 StartY=-157.032 StartZ=0 EndX=194.75 EndY=-157.032 EndZ=0
    g359: Circle CenterX=249.36 CenterY=-157.032 CenterZ=0 NormalX=0 NormalY=0 NormalZ=1 AngleXU=0 Radius=3.175
    g360: LineSegment StartX=194.75 StartY=-157.032 StartZ=0 EndX=249.36 EndY=-157.032 EndZ=0
    g361: Circle CenterX=303.97 CenterY=-157.032 CenterZ=0 NormalX=0 NormalY=0 NormalZ=1 AngleXU=0 Radius=3.175
    g362: LineSegment StartX=249.36 StartY=-157.032 StartZ=0 EndX=303.97 EndY=-157.032 EndZ=0
    g363: LineSegment StartX=-405.961 StartY=-157.032 StartZ=0 EndX=-405.961 EndY=-207.832 EndZ=0
    g364: LineSegment StartX=-405.96 StartY=-207.832 StartZ=0 EndX=-351.35 EndY=-207.832 EndZ=0
    g365: Circle CenterX=-296.74 CenterY=-207.832 CenterZ=0 NormalX=0 NormalY=0 NormalZ=1 AngleXU=0 Radius=3.175
    g366: LineSegment StartX=-351.35 StartY=-207.832 StartZ=0 EndX=-296.74 EndY=-207.832 EndZ=0
    g367: Circle CenterX=-242.13 CenterY=-207.832 CenterZ=0 NormalX=0 NormalY=0 NormalZ=1 AngleXU=0 Radius=3.175
    g368: LineSegment StartX=-296.74 StartY=-207.832 StartZ=0 EndX=-242.13 EndY=-207.832 EndZ=0
    g369: Circle CenterX=-187.52 CenterY=-207.832 CenterZ=0 NormalX=0 NormalY=0 NormalZ=1 AngleXU=0 Radius=3.175
    g370: LineSegment StartX=-242.13 StartY=-207.832 StartZ=0 EndX=-187.52 EndY=-207.832 EndZ=0
    g371: Circle CenterX=-132.91 CenterY=-207.832 CenterZ=0 NormalX=0 NormalY=0 NormalZ=1 AngleXU=0 Radius=3.175
    g372: LineSegment StartX=-187.52 StartY=-207.832 StartZ=0 EndX=-132.91 EndY=-207.832 EndZ=0
    g373: Circle CenterX=-78.3004 CenterY=-207.832 CenterZ=0 NormalX=0 NormalY=0 NormalZ=1 AngleXU=0 Radius=3.175
    g374: LineSegment StartX=-132.91 StartY=-207.832 StartZ=0 EndX=-78.3004 EndY=-207.832 EndZ=0
    g375: Circle CenterX=-23.6904 CenterY=-207.832 CenterZ=0 NormalX=0 NormalY=0 NormalZ=1 AngleXU=0 Radius=3.175
    g376: LineSegment StartX=-78.3004 StartY=-207.832 StartZ=0 EndX=-23.6904 EndY=-207.832 EndZ=0
    g377: Circle CenterX=30.9196 CenterY=-207.832 CenterZ=0 NormalX=0 NormalY=0 NormalZ=1 AngleXU=0 Radius=3.175
    g378: LineSegment StartX=-23.6904 StartY=-207.832 StartZ=0 EndX=30.9196 EndY=-207.832 EndZ=0
    g379: Circle CenterX=85.5296 CenterY=-207.832 CenterZ=0 NormalX=0 NormalY=0 NormalZ=1 AngleXU=0 Radius=3.175
    g380: LineSegment StartX=30.9196 StartY=-207.832 StartZ=0 EndX=85.5296 EndY=-207.832 EndZ=0
    g381: Circle CenterX=140.14 CenterY=-207.832 CenterZ=0 NormalX=0 NormalY=0 NormalZ=1 AngleXU=0 Radius=3.175
    g382: LineSegment StartX=85.5296 StartY=-207.832 StartZ=0 EndX=140.14 EndY=-207.832 EndZ=0
    g383: Circle CenterX=194.75 CenterY=-207.832 CenterZ=0 NormalX=0 NormalY=0 NormalZ=1 AngleXU=0 Radius=3.175
    g384: LineSegment StartX=140.14 StartY=-207.832 StartZ=0 EndX=194.75 EndY=-207.832 EndZ=0
    g385: Circle CenterX=249.36 CenterY=-207.832 CenterZ=0 NormalX=0 NormalY=0 NormalZ=1 AngleXU=0 Radius=3.175
    g386: LineSegment StartX=194.75 StartY=-207.832 StartZ=0 EndX=249.36 EndY=-207.832 EndZ=0
    g387: Circle CenterX=303.97 CenterY=-207.832 CenterZ=0 NormalX=0 NormalY=0 NormalZ=1 AngleXU=0 Radius=3.175
    g388: LineSegment StartX=249.36 StartY=-207.832 StartZ=0 EndX=303.97 EndY=-207.832 EndZ=0
  constraints (968):
    c: Coincident(g0,g1)
    c: Coincident(g1,g2)
    c: Coincident(g2,g3)
    c: Coincident(g3,g0)
    c: Horizontal(g0)
    c: Horizontal(g2)
    c: Vertical(g1)
    c: Vertical(g3)
    c: Distance(g0) = 777.875
    c: Distance(g3) = 711.2
    c: Distance(g4,g3) = 33.9852
    c: Distance(g4,g0) = 25.4
    c: Diameter(g4) = 6.35
    c: Diameter(g5) = 6.35
    c: Coincident(g4,g6)
    c: Coincident(g5,g6)
    c: Distance(g6) = 54.61
    c: Angle(g6) = 0
    c: Diameter(g7) = 6.35
    c: Coincident(g5,g8)
    c: Coincident(g7,g8)
    c: Equal(g6,g8)
    c: Parallel(g8,g6)
    c: Diameter(g9) = 6.35
    c: Coincident(g7,g10)
    c: Coincident(g9,g10)
    c: Equal(g6,g10)
    c: Parallel(g10,g6)
    c: Diameter(g11) = 6.35
    c: Coincident(g9,g12)
    c: Coincident(g11,g12)
    c: Equal(g6,g12)
    c: Parallel(g12,g6)
    c: Diameter(g13) = 6.35
    c: Coincident(g11,g14)
    c: Coincident(g13,g14)
    c: Equal(g6,g14)
    c: Parallel(g14,g6)
    c: Diameter(g15) = 6.35
    c: Coincident(g13,g16)
    c: Coincident(g15,g16)
    c: Equal(g6,g16)
    c: Parallel(g16,g6)
    c: Diameter(g17) = 6.35
    c: Coincident(g15,g18)
    c: Coincident(g17,g18)
    c: Equal(g6,g18)
    c: Parallel(g18,g6)
    c: Diameter(g19) = 6.35
    c: Coincident(g17,g20)
    c: Coincident(g19,g20)
    c: Equal(g6,g20)
    c: Parallel(g20,g6)
    c: Diameter(g21) = 6.35
    c: Coincident(g19,g22)
    c: Coincident(g21,g22)
    c: Equal(g6,g22)
    c: Parallel(g22,g6)
    c: Diameter(g23) = 6.35
    c: Coincident(g21,g24)
    c: Coincident(g23,g24)
    c: Equal(g6,g24)
    c: Parallel(g24,g6)
    c: Diameter(g25) = 6.35
    c: Coincident(g23,g26)
    c: Coincident(g25,g26)
    c: Equal(g6,g26)
    c: Parallel(g26,g6)
    c: Diameter(g27) = 6.35
    c: Coincident(g25,g28)
    c: Coincident(g27,g28)
    c: Equal(g6,g28)
    c: Parallel(g28,g6)
    c: Diameter(g29) = 6.35
    c: Coincident(g27,g30)
    c: Coincident(g29,g30)
    c: Equal(g6,g30)
    c: Parallel(g30,g6)
    c: Diameter(g31) = 6.35
    c: Coincident(g4,g32)
    c: Coincident(g31,g32)
    c: Distance(g32) = 50.8
    c: Perpendicular(g32,g6)
    c: Diameter(g33) = 6.35
    c: Coincident(g31,g34)
    c: Coincident(g33,g34)
    c: Equal(g6,g34)
    c: Parallel(g34,g6)
    c: Diameter(g35) = 6.35
    c: Coincident(g33,g36)
    c: Coincident(g35,g36)
    c: Equal(g6,g36)
    c: Parallel(g36,g6)
    c: Diameter(g37) = 6.35
    c: Coincident(g35,g38)
    c: Coincident(g37,g38)
    c: Equal(g6,g38)
    c: Parallel(g38,g6)
    c: Diameter(g39) = 6.35
    c: Coincident(g37,g40)
    c: Coincident(g39,g40)
    c: Equal(g6,g40)
    c: Parallel(g40,g6)
    c: Diameter(g41) = 6.35
    c: Coincident(g39,g42)
    c: Coincident(g41,g42)
    c: Equal(g6,g42)
    c: Parallel(g42,g6)
    c: Diameter(g43) = 6.35
    c: Coincident(g41,g44)
    c: Coincident(g43,g44)
    c: Equal(g6,g44)
    c: Parallel(g44,g6)
    c: Diameter(g45) = 6.35
    c: Coincident(g43,g46)
    c: Coincident(g45,g46)
    c: Equal(g6,g46)
    c: Parallel(g46,g6)
    c: Diameter(g47) = 6.35
    c: Coincident(g45,g48)
    c: Coincident(g47,g48)
    c: Equal(g6,g48)
    c: Parallel(g48,g6)
    c: Diameter(g49) = 6.35
    c: Coincident(g47,g50)
    c: Coincident(g49,g50)
    c: Equal(g6,g50)
    c: Parallel(g50,g6)
    c: Diameter(g51) = 6.35
    c: Coincident(g49,g52)
    c: Coincident(g51,g52)
    c: Equal(g6,g52)
    c: Parallel(g52,g6)
    c: Diameter(g53) = 6.35
    c: Coincident(g51,g54)
    c: Coincident(g53,g54)
    c: Equal(g6,g54)
    c: Parallel(g54,g6)
    c: Diameter(g55) = 6.35
    c: Coincident(g53,g56)
    c: Coincident(g55,g56)
    c: Equal(g6,g56)
    c: Parallel(g56,g6)
    c: Diameter(g57) = 6.35
    c: Coincident(g55,g58)
    c: Coincident(g57,g58)
    c: Equal(g6,g58)
    c: Parallel(g58,g6)
    c: Diameter(g59) = 6.35
    c: Coincident(g31,g60)
    c: Coincident(g59,g60)
    c: Equal(g32,g60)
    c: Perpendicular(g60,g6)
    c: Diameter(g61) = 6.35
    c: Coincident(g59,g62)
    c: Coincident(g61,g62)
    c: Equal(g6,g62)
    c: Parallel(g62,g6)
    c: Diameter(g63) = 6.35
    c: Coincident(g61,g64)
    c: Coincident(g63,g64)
    c: Equal(g6,g64)
    c: Parallel(g64,g6)
    c: Diameter(g65) = 6.35
    c: Coincident(g63,g66)
    c: Coincident(g65,g66)
    c: Equal(g6,g66)
    c: Parallel(g66,g6)
    c: Diameter(g67) = 6.35
    c: Coincident(g65,g68)
    c: Coincident(g67,g68)
    c: Equal(g6,g68)
    c: Parallel(g68,g6)
    c: Diameter(g69) = 6.35
    c: Coincident(g67,g70)
    c: Coincident(g69,g70)
    c: Equal(g6,g70)
    c: Parallel(g70,g6)
    c: Diameter(g71) = 6.35
    c: Coincident(g69,g72)
    c: Coincident(g71,g72)
    c: Equal(g6,g72)
    c: Parallel(g72,g6)
    c: Diameter(g73) = 6.35
    c: Coincident(g71,g74)
    c: Coincident(g73,g74)
    c: Equal(g6,g74)
    c: Parallel(g74,g6)
    c: Diameter(g75) = 6.35
    c: Coincident(g73,g76)
    c: Coincident(g75,g76)
    c: Equal(g6,g76)
    c: Parallel(g76,g6)
    c: Diameter(g77) = 6.35
    c: Coincident(g75,g78)
    c: Coincident(g77,g78)
    c: Equal(g6,g78)
    c: Parallel(g78,g6)
    c: Diameter(g79) = 6.35
    c: Coincident(g77,g80)
    c: Coincident(g79,g80)
    c: Equal(g6,g80)
    c: Parallel(g80,g6)
    c: Diameter(g81) = 6.35
    c: Coincident(g79,g82)
    c: Coincident(g81,g82)
    c: Equal(g6,g82)
    c: Parallel(g82,g6)
    c: Diameter(g83) = 6.35
    c: Coincident(g81,g84)
    c: Coincident(g83,g84)
    c: Equal(g6,g84)
    c: Parallel(g84,g6)
    c: Diameter(g85) = 6.35
    c: Coincident(g83,g86)
    c: Coincident(g85,g86)
    c: Equal(g6,g86)
    c: Parallel(g86,g6)
    c: Diameter(g87) = 6.35
    c: Coincident(g59,g88)
    c: Coincident(g87,g88)
    c: Equal(g32,g88)
    c: Perpendicular(g88,g6)
    c: Diameter(g89) = 6.35
    c: Coincident(g87,g90)
    c: Coincident(g89,g90)
    c: Equal(g6,g90)
    c: Parallel(g90,g6)
    c: Diameter(g91) = 6.35
    c: Coincident(g89,g92)
    c: Coincident(g91,g92)
    c: Equal(g6,g92)
    c: Parallel(g92,g6)
    c: Diameter(g93) = 6.35
    c: Coincident(g91,g94)
    c: Coincident(g93,g94)
    c: Equal(g6,g94)
    c: Parallel(g94,g6)
    c: Diameter(g95) = 6.35
    c: Coincident(g93,g96)
    c: Coincident(g95,g96)
    c: Equal(g6,g96)
    c: Parallel(g96,g6)
    c: Diameter(g97) = 6.35
    c: Coincident(g95,g98)
    c: Coincident(g97,g98)
    c: Equal(g6,g98)
    c: Parallel(g98,g6)
    c: Diameter(g99) = 6.35
    c: Coincident(g97,g100)
    c: Coincident(g99,g100)
    c: Equal(g6,g100)
    c: Parallel(g100,g6)
    c: Diameter(g101) = 6.35
    c: Coincident(g99,g102)
    c: Coincident(g101,g102)
    c: Equal(g6,g102)
    c: Parallel(g102,g6)
    c: Diameter(g103) = 6.35
    c: Coincident(g101,g104)
    c: Coincident(g103,g104)
    c: Equal(g6,g104)
    c: Parallel(g104,g6)
    c: Diameter(g105) = 6.35
    c: Coincident(g103,g106)
    c: Coincident(g105,g106)
    c: Equal(g6,g106)
    c: Parallel(g106,g6)
    c: Diameter(g107) = 6.35
    c: Coincident(g105,g108)
    c: Coincident(g107,g108)
    c: Equal(g6,g108)
    c: Parallel(g108,g6)
    c: Diameter(g109) = 6.35
    c: Coincident(g107,g110)
    c: Coincident(g109,g110)
    c: Equal(g6,g110)
    c: Parallel(g110,g6)
    c: Diameter(g111) = 6.35
    c: Coincident(g109,g112)
    c: Coincident(g111,g112)
    c: Equal(g6,g112)
    c: Parallel(g112,g6)
    c: Diameter(g113) = 6.35
    c: Coincident(g111,g114)
    c: Coincident(g113,g114)
    c: Equal(g6,g114)
    c: Parallel(g114,g6)
    c: Diameter(g115) = 6.35
    c: Coincident(g87,g116)
    c: Coincident(g115,g116)
    c: Equal(g32,g116)
    c: Perpendicular(g116,g6)
    c: Diameter(g117) = 6.35
    c: Coincident(g115,g118)
    c: Coincident(g117,g118)
    c: Equal(g6,g118)
    c: Parallel(g118,g6)
    c: Diameter(g119) = 6.35
    c: Coincident(g117,g120)
    c: Coincident(g119,g120)
    c: Equal(g6,g120)
    c: Parallel(g120,g6)
    c: Diameter(g121) = 6.35
    c: Coincident(g119,g122)
    c: Coincident(g121,g122)
    c: Equal(g6,g122)
    c: Parallel(g122,g6)
    c: Diameter(g123) = 6.35
    c: Coincident(g121,g124)
    c: Coincident(g123,g124)
    c: Equal(g6,g124)
    c: Parallel(g124,g6)
    c: Diameter(g125) = 6.35
    c: Coincident(g123,g126)
    c: Coincident(g125,g126)
    c: Equal(g6,g126)
    c: Parallel(g126,g6)
    c: Diameter(g127) = 6.35
    c: Coincident(g125,g128)
    c: Coincident(g127,g128)
    c: Equal(g6,g128)
    c: Parallel(g128,g6)
    c: Diameter(g129) = 6.35
    c: Coincident(g127,g130)
    c: Coincident(g129,g130)
    c: Equal(g6,g130)
    c: Parallel(g130,g6)
    c: Diameter(g131) = 6.35
    c: Coincident(g129,g132)
    c: Coincident(g131,g132)
    c: Equal(g6,g132)
    c: Parallel(g132,g6)
    c: Diameter(g133) = 6.35
    c: Coincident(g131,g134)
    c: Coincident(g133,g134)
    c: Equal(g6,g134)
    c: Parallel(g134,g6)
    c: Diameter(g135) = 6.35
    c: Coincident(g133,g136)
    c: Coincident(g135,g136)
    c: Equal(g6,g136)
    c: Parallel(g136,g6)
    c: Diameter(g137) = 6.35
    c: Coincident(g135,g138)
    c: Coincident(g137,g138)
    c: Equal(g6,g138)
    c: Parallel(g138,g6)
    c: Diameter(g139) = 6.35
    c: Coincident(g137,g140)
    c: Coincident(g139,g140)
    c: Equal(g6,g140)
    c: Parallel(g140,g6)
    c: Diameter(g141) = 6.35
    c: Coincident(g139,g142)
    c: Coincident(g141,g142)
    c: Equal(g6,g142)
    c: Parallel(g142,g6)
    c: Diameter(g143) = 6.35
    c: Coincident(g115,g144)
    c: Coincident(g143,g144)
    c: Equal(g32,g144)
    c: Perpendicular(g144,g6)
    c: Diameter(g145) = 6.35
    c: Coincident(g143,g146)
    c: Coincident(g145,g146)
    c: Equal(g6,g146)
    c: Parallel(g146,g6)
    c: Diameter(g147) = 6.35
    c: Coincident(g145,g148)
    c: Coincident(g147,g148)
    c: Equal(g6,g148)
    c: Parallel(g148,g6)
    c: Diameter(g149) = 6.35
    c: Coincident(g147,g150)
    c: Coincident(g149,g150)
    c: Equal(g6,g150)
    c: Parallel(g150,g6)
    c: Diameter(g151) = 6.35
    c: Coincident(g149,g152)
    c: Coincident(g151,g152)
    c: Equal(g6,g152)
    c: Parallel(g152,g6)
    c: Diameter(g153) = 6.35
    c: Coincident(g151,g154)
    c: Coincident(g153,g154)
    c: Equal(g6,g154)
    c: Parallel(g154,g6)
    c: Diameter(g155) = 6.35
    c: Coincident(g153,g156)
    c: Coincident(g155,g156)
    c: Equal(g6,g156)
    c: Parallel(g156,g6)
    c: Diameter(g157) = 6.35
    c: Coincident(g155,g158)
    c: Coincident(g157,g158)
    c: Equal(g6,g158)
    c: Parallel(g158,g6)
    c: Diameter(g159) = 6.35
    c: Coincident(g157,g160)
    c: Coincident(g159,g160)
    c: Equal(g6,g160)
    c: Parallel(g160,g6)
    c: Diameter(g161) = 6.35
    c: Coincident(g159,g162)
    c: Coincident(g161,g162)
    c: Equal(g6,g162)
    c: Parallel(g162,g6)
    c: Diameter(g163) = 6.35
    c: Coincident(g161,g164)
    c: Coincident(g163,g164)
    c: Equal(g6,g164)
    c: Parallel(g164,g6)
    c: Diameter(g165) = 6.35
    c: Coincident(g163,g166)
    c: Coincident(g165,g166)
    c: Equal(g6,g166)
    c: Parallel(g166,g6)
    c: Diameter(g167) = 6.35
    c: Coincident(g165,g168)
    c: Coincident(g167,g168)
    c: Equal(g6,g168)
    c: Parallel(g168,g6)
    c: Diameter(g169) = 6.35
    c: Coincident(g167,g170)
    c: Coincident(g169,g170)
    c: Equal(g6,g170)
    c: Parallel(g170,g6)
    c: Diameter(g171) = 6.35
    c: Coincident(g143,g172)
    c: Coincident(g171,g172)
    c: Equal(g32,g172)
    c: Perpendicular(g172,g6)
    c: Diameter(g173) = 6.35
    c: Coincident(g171,g174)
    c: Coincident(g173,g174)
    c: Equal(g6,g174)
    c: Parallel(g174,g6)
    c: Diameter(g175) = 6.35
    c: Coincident(g173,g176)
    c: Coincident(g175,g176)
    c: Equal(g6,g176)
    c: Parallel(g176,g6)
    c: Diameter(g177) = 6.35
    c: Coincident(g175,g178)
    c: Coincident(g177,g178)
    c: Equal(g6,g178)
    c: Parallel(g178,g6)
    c: Diameter(g179) = 6.35
    c: Coincident(g177,g180)
    c: Coincident(g179,g180)
    c: Equal(g6,g180)
    c: Parallel(g180,g6)
    c: Diameter(g181) = 6.35
    c: Coincident(g179,g182)
    c: Coincident(g181,g182)
    c: Equal(g6,g182)
    c: Parallel(g182,g6)
    c: Diameter(g183) = 6.35
    c: Coincident(g181,g184)
    c: Coincident(g183,g184)
    c: Equal(g6,g184)
    c: Parallel(g184,g6)
    c: Diameter(g185) = 6.35
    c: Coincident(g183,g186)
    c: Coincident(g185,g186)
    c: Equal(g6,g186)
    c: Parallel(g186,g6)
    c: Diameter(g187) = 6.35
    c: Coincident(g185,g188)
    c: Coincident(g187,g188)
    c: Equal(g6,g188)
    c: Parallel(g188,g6)
    c: Diameter(g189) = 6.35
    c: Coincident(g187,g190)
    c: Coincident(g189,g190)
    c: Equal(g6,g190)
    c: Parallel(g190,g6)
    c: Diameter(g191) = 6.35
    c: Coincident(g189,g192)
    c: Coincident(g191,g192)
    c: Equal(g6,g192)
    c: Parallel(g192,g6)
    c: Diameter(g193) = 6.35
    c: Coincident(g191,g194)
    c: Coincident(g193,g194)
    c: Equal(g6,g194)
    c: Parallel(g194,g6)
    c: Diameter(g195) = 6.35
    c: Coincident(g193,g196)
    c: Coincident(g195,g196)
    c: Equal(g6,g196)
    c: Parallel(g196,g6)
    c: Diameter(g197) = 6.35
    c: Coincident(g195,g198)
    c: Coincident(g197,g198)
    c: Equal(g6,g198)
    c: Parallel(g198,g6)
    c: Diameter(g199) = 6.35
    c: Coincident(g171,g200)
    c: Coincident(g199,g200)
    c: Equal(g32,g200)
    c: Perpendicular(g200,g6)
    c: Diameter(g201) = 6.35
    c: Coincident(g199,g202)
    c: Coincident(g201,g202)
    c: Equal(g6,g202)
    c: Parallel(g202,g6)
    c: Diameter(g203) = 6.35
    c: Coincident(g201,g204)
    c: Coincident(g203,g204)
    c: Equal(g6,g204)
    c: Parallel(g204,g6)
    c: Diameter(g205) = 6.35
    c: Coincident(g203,g206)
    c: Coincident(g205,g206)
    c: Equal(g6,g206)
    c: Parallel(g206,g6)
    c: Diameter(g207) = 6.35
    c: Coincident(g205,g208)
    c: Coincident(g207,g208)
    c: Equal(g6,g208)
    c: Parallel(g208,g6)
    c: Diameter(g209) = 6.35
    c: Coincident(g207,g210)
    c: Coincident(g209,g210)
    c: Equal(g6,g210)
    c: Parallel(g210,g6)
    c: Diameter(g211) = 6.35
    c: Coincident(g209,g212)
    c: Coincident(g211,g212)
    c: Equal(g6,g212)
    c: Parallel(g212,g6)
    c: Diameter(g213) = 6.35
    c: Coincident(g211,g214)
    c: Coincident(g213,g214)
    c: Equal(g6,g214)
    c: Parallel(g214,g6)
    c: Diameter(g215) = 6.35
    c: Coincident(g213,g216)
    c: Coincident(g215,g216)
    c: Equal(g6,g216)
    c: Parallel(g216,g6)
    c: Diameter(g217) = 6.35
    c: Coincident(g215,g218)
    c: Coincident(g217,g218)
    c: Equal(g6,g218)
    c: Parallel(g218,g6)
    c: Diameter(g219) = 6.35
    c: Coincident(g217,g220)
    c: Coincident(g219,g220)
    c: Equal(g6,g220)
    c: Parallel(g220,g6)
    c: Diameter(g221) = 6.35
    c: Coincident(g219,g222)
    c: Coincident(g221,g222)
    c: Equal(g6,g222)
    c: Parallel(g222,g6)
    c: Diameter(g223) = 6.35
    c: Coincident(g221,g224)
    c: Coincident(g223,g224)
    c: Equal(g6,g224)
    c: Parallel(g224,g6)
    c: Diameter(g225) = 6.35
    c: Coincident(g223,g226)
    c: Coincident(g225,g226)
    c: Equal(g6,g226)
    c: Parallel(g226,g6)
    c: Diameter(g227) = 6.35
    c: Coincident(g199,g228)
    c: Coincident(g227,g228)
    c: Equal(g32,g228)
    c: Perpendicular(g228,g6)
    c: Diameter(g229) = 6.35
    c: Coincident(g227,g230)
    c: Coincident(g229,g230)
    c: Equal(g6,g230)
    c: Parallel(g230,g6)
    c: Diameter(g231) = 6.35
    c: Coincident(g229,g232)
    c: Coincident(g231,g232)
    c: Equal(g6,g232)
    c: Parallel(g232,g6)
    c: Diameter(g233) = 6.35
    c: Coincident(g231,g234)
    c: Coincident(g233,g234)
    c: Equal(g6,g234)
    c: Parallel(g234,g6)
    c: Diameter(g235) = 6.35
    c: Coincident(g233,g236)
    c: Coincident(g235,g236)
    c: Equal(g6,g236)
    c: Parallel(g236,g6)
    c: Diameter(g237) = 6.35
    c: Coincident(g235,g238)
    c: Coincident(g237,g238)
    c: Equal(g6,g238)
    c: Parallel(g238,g6)
    c: Diameter(g239) = 6.35
    c: Coincident(g237,g240)
    c: Coincident(g239,g240)
    c: Equal(g6,g240)
    c: Parallel(g240,g6)
    c: Diameter(g241) = 6.35
    c: Coincident(g239,g242)
    c: Coincident(g241,g242)
    c: Equal(g6,g242)
    c: Parallel(g242,g6)
    c: Diameter(g243) = 6.35
    c: Coincident(g241,g244)
    c: Coincident(g243,g244)
    c: Equal(g6,g244)
    c: Parallel(g244,g6)
    c: Diameter(g245) = 6.35
    c: Coincident(g243,g246)
    c: Coincident(g245,g246)
    c: Equal(g6,g246)
    c: Parallel(g246,g6)
    c: Diameter(g247) = 6.35
    c: Coincident(g245,g248)
    c: Coincident(g247,g248)
    c: Equal(g6,g248)
    c: Parallel(g248,g6)
    c: Diameter(g249) = 6.35
    c: Coincident(g247,g250)
    c: Coincident(g249,g250)
    c: Equal(g6,g250)
    c: Parallel(g250,g6)
    c: Diameter(g251) = 6.35
    c: Coincident(g249,g252)
    c: Coincident(g251,g252)
    c: Equal(g6,g252)
    c: Parallel(g252,g6)
    c: Diameter(g253) = 6.35
    c: Coincident(g251,g254)
    c: Coincident(g253,g254)
    c: Equal(g6,g254)
    c: Parallel(g254,g6)
    c: Diameter(g255) = 6.35
    c: Coincident(g227,g256)
    c: Coincident(g255,g256)
    c: Equal(g32,g256)
    c: Perpendicular(g256,g6)
    c: Diameter(g257) = 6.35
    c: Coincident(g255,g258)
    c: Coincident(g257,g258)
    c: Equal(g6,g258)
    c: Parallel(g258,g6)
    c: Diameter(g259) = 6.35
    c: Coincident(g257,g260)
    c: Coincident(g259,g260)
    c: Equal(g6,g260)
    c: Parallel(g260,g6)
    c: Diameter(g261) = 6.35
    c: Coincident(g259,g262)
    c: Coincident(g261,g262)
    c: Equal(g6,g262)
    c: Parallel(g262,g6)
    c: Diameter(g263) = 6.35
    c: Coincident(g261,g264)
    c: Coincident(g263,g264)
    c: Equal(g6,g264)
    c: Parallel(g264,g6)
    c: Diameter(g265) = 6.35
    c: Coincident(g263,g266)
    c: Coincident(g265,g266)
    c: Equal(g6,g266)
    c: Parallel(g266,g6)
    c: Diameter(g267) = 6.35
    c: Coincident(g265,g268)
    c: Coincident(g267,g268)
    c: Equal(g6,g268)
    c: Parallel(g268,g6)
    c: Diameter(g269) = 6.35
    c: Coincident(g267,g270)
    c: Coincident(g269,g270)
    c: Equal(g6,g270)
    c: Parallel(g270,g6)
    c: Diameter(g271) = 6.35
    c: Coincident(g269,g272)
    c: Coincident(g271,g272)
    c: Equal(g6,g272)
    c: Parallel(g272,g6)
    c: Diameter(g273) = 6.35
    c: Coincident(g271,g274)
    c: Coincident(g273,g274)
    c: Equal(g6,g274)
    c: Parallel(g274,g6)
    c: Diameter(g275) = 6.35
    c: Coincident(g273,g276)
    c: Coincident(g275,g276)
    c: Equal(g6,g276)
    c: Parallel(g276,g6)
    c: Diameter(g277) = 6.35
    c: Coincident(g275,g278)
    c: Coincident(g277,g278)
    c: Equal(g6,g278)
    c: Parallel(g278,g6)
    c: Diameter(g279) = 6.35
    c: Coincident(g277,g280)
    c: Coincident(g279,g280)
    c: Equal(g6,g280)
    c: Parallel(g280,g6)
    c: Diameter(g281) = 6.35
    c: Coincident(g279,g282)
    c: Coincident(g281,g282)
    c: Equal(g6,g282)
    c: Parallel(g282,g6)
    c: Diameter(g283) = 6.35
    c: Coincident(g255,g284)
    c: Coincident(g283,g284)
    c: Equal(g32,g284)
    c: Perpendicular(g284,g6)
    c: Diameter(g285) = 6.35
    c: Coincident(g283,g286)
    c: Coincident(g285,g286)
    c: Equal(g6,g286)
    c: Parallel(g286,g6)
    c: Diameter(g287) = 6.35
    c: Coincident(g285,g288)
    c: Coincident(g287,g288)
    c: Equal(g6,g288)
    c: Parallel(g288,g6)
    c: Diameter(g289) = 6.35
    c: Coincident(g287,g290)
    c: Coincident(g289,g290)
    c: Equal(g6,g290)
    c: Parallel(g290,g6)
    c: Diameter(g291) = 6.35
    c: Coincident(g289,g292)
    c: Coincident(g291,g292)
    c: Equal(g6,g292)
    c: Parallel(g292,g6)
    c: Diameter(g293) = 6.35
    c: Coincident(g291,g294)
    c: Coincident(g293,g294)
    c: Equal(g6,g294)
    c: Parallel(g294,g6)
    c: Diameter(g295) = 6.35
    c: Coincident(g293,g296)
    c: Coincident(g295,g296)
    c: Equal(g6,g296)
    c: Parallel(g296,g6)
    c: Diameter(g297) = 6.35
    c: Coincident(g295,g298)
    c: Coincident(g297,g298)
    c: Equal(g6,g298)
    c: Parallel(g298,g6)
    c: Diameter(g299) = 6.35
    c: Coincident(g297,g300)
    c: Coincident(g299,g300)
    c: Equal(g6,g300)
    c: Parallel(g300,g6)
    c: Diameter(g301) = 6.35
    c: Coincident(g299,g302)
    c: Coincident(g301,g302)
    c: Equal(g6,g302)
    c: Parallel(g302,g6)
    c: Diameter(g303) = 6.35
    c: Coincident(g301,g304)
    c: Coincident(g303,g304)
    c: Equal(g6,g304)
    c: Parallel(g304,g6)
    c: Diameter(g305) = 6.35
    c: Coincident(g303,g306)
    c: Coincident(g305,g306)
    c: Equal(g6,g306)
    c: Parallel(g306,g6)
    c: Diameter(g307) = 6.35
    c: Coincident(g305,g308)
    c: Coincident(g307,g308)
    c: Equal(g6,g308)
    c: Parallel(g308,g6)
    c: Diameter(g309) = 6.35
    c: Coincident(g307,g310)
    c: Coincident(g309,g310)
    c: Equal(g6,g310)
    c: Parallel(g310,g6)
    c: Coincident(g283,g311)
    c: Equal(g32,g311)
    c: Perpendicular(g311,g6)
    c: Equal(g6,g312)
    c: Parallel(g312,g6)
    c: Diameter(g313) = 6.35
    c: Coincident(g313,g314)
    c: Equal(g6,g314)
    c: Parallel(g314,g6)
    c: Diameter(g315) = 6.35
    c: Coincident(g313,g316)
    c: Coincident(g315,g316)
    c: Equal(g6,g316)
    c: Parallel(g316,g6)
    c: Diameter(g317) = 6.35
    c: Coincident(g315,g318)
    c: Coincident(g317,g318)
    c: Equal(g6,g318)
    c: Parallel(g318,g6)
    c: Diameter(g319) = 6.35
    c: Coincident(g317,g320)
    c: Coincident(g319,g320)
    c: Equal(g6,g320)
    c: Parallel(g320,g6)
    c: Diameter(g321) = 6.35
    c: Coincident(g319,g322)
    c: Coincident(g321,g322)
    c: Equal(g6,g322)
    c: Parallel(g322,g6)
    c: Diameter(g323) = 6.35
    c: Coincident(g321,g324)
    c: Coincident(g323,g324)
    c: Equal(g6,g324)
    c: Parallel(g324,g6)
    c: Diameter(g325) = 6.35
    c: Coincident(g323,g326)
    c: Coincident(g325,g326)
    c: Equal(g6,g326)
    c: Parallel(g326,g6)
    c: Diameter(g327) = 6.35
    c: Coincident(g325,g328)
    c: Coincident(g327,g328)
    c: Equal(g6,g328)
    c: Parallel(g328,g6)
    c: Diameter(g329) = 6.35
    c: Coincident(g327,g330)
    c: Coincident(g329,g330)
    c: Equal(g6,g330)
    c: Parallel(g330,g6)
    c: Diameter(g331) = 6.35
    c: Coincident(g329,g332)
    c: Coincident(g331,g332)
    c: Equal(g6,g332)
    c: Parallel(g332,g6)
    c: Diameter(g333) = 6.35
    c: Coincident(g331,g334)
    c: Coincident(g333,g334)
    c: Equal(g6,g334)
    c: Parallel(g334,g6)
    c: Diameter(g335) = 6.35
    c: Coincident(g333,g336)
    c: Coincident(g335,g336)
    c: Equal(g6,g336)
    c: Parallel(g336,g6)
    c: Equal(g32,g337)
    c: Perpendicular(g337,g6)
    c: Equal(g6,g338)
    c: Parallel(g338,g6)
    c: Diameter(g339) = 6.35
    c: Coincident(g339,g340)
    c: Equal(g6,g340)
    c: Parallel(g340,g6)
    c: Diameter(g341) = 6.35
    c: Coincident(g339,g342)
    c: Coincident(g341,g342)
    c: Equal(g6,g342)
    c: Parallel(g342,g6)
    c: Diameter(g343) = 6.35
    c: Coincident(g341,g344)
    c: Coincident(g343,g344)
    c: Equal(g6,g344)
    c: Parallel(g344,g6)
    c: Diameter(g345) = 6.35
    c: Coincident(g343,g346)
    c: Coincident(g345,g346)
    c: Equal(g6,g346)
    c: Parallel(g346,g6)
    c: Diameter(g347) = 6.35
    c: Coincident(g345,g348)
    c: Coincident(g347,g348)
    c: Equal(g6,g348)
    c: Parallel(g348,g6)
    c: Diameter(g349) = 6.35
    c: Coincident(g347,g350)
    c: Coincident(g349,g350)
    c: Equal(g6,g350)
    c: Parallel(g350,g6)
    c: Diameter(g351) = 6.35
    c: Coincident(g349,g352)
    c: Coincident(g351,g352)
    c: Equal(g6,g352)
    c: Parallel(g352,g6)
    c: Diameter(g353) = 6.35
    c: Coincident(g351,g354)
    c: Coincident(g353,g354)
    c: Equal(g6,g354)
    c: Parallel(g354,g6)
    c: Diameter(g355) = 6.35
    c: Coincident(g353,g356)
    c: Coincident(g355,g356)
    c: Equal(g6,g356)
    c: Parallel(g356,g6)
    c: Diameter(g357) = 6.35
    c: Coincident(g355,g358)
    c: Coincident(g357,g358)
    c: Equal(g6,g358)
    c: Parallel(g358,g6)
    c: Diameter(g359) = 6.35
    c: Coincident(g357,g360)
    c: Coincident(g359,g360)
    c: Equal(g6,g360)
    c: Parallel(g360,g6)
    c: Diameter(g361) = 6.35
    c: Coincident(g359,g362)
    c: Coincident(g361,g362)
    c: Equal(g6,g362)
    c: Parallel(g362,g6)
    c: Equal(g32,g363)
    c: Perpendicular(g363,g6)
    c: Equal(g6,g364)
    c: Parallel(g364,g6)
    c: Diameter(g365) = 6.35
    c: Coincident(g365,g366)
    c: Equal(g6,g366)
    c: Parallel(g366,g6)
    c: Diameter(g367) = 6.35
    c: Coincident(g365,g368)
    c: Coincident(g367,g368)
    c: Equal(g6,g368)
    c: Parallel(g368,g6)
    c: Diameter(g369) = 6.35
    c: Coincident(g367,g370)
    c: Coincident(g369,g370)
    c: Equal(g6,g370)
    c: Parallel(g370,g6)
    c: Diameter(g371) = 6.35
    c: Coincident(g369,g372)
    c: Coincident(g371,g372)
    c: Equal(g6,g372)
    c: Parallel(g372,g6)
    c: Diameter(g373) = 6.35
    c: Coincident(g371,g374)
    c: Coincident(g373,g374)
    c: Equal(g6,g374)
    c: Parallel(g374,g6)
    c: Diameter(g375) = 6.35
    c: Coincident(g373,g376)
    c: Coincident(g375,g376)
    c: Equal(g6,g376)
    c: Parallel(g376,g6)
    c: Diameter(g377) = 6.35
    c: Coincident(g375,g378)
    c: Coincident(g377,g378)
    c: Equal(g6,g378)
    c: Parallel(g378,g6)
    c: Diameter(g379) = 6.35
    c: Coincident(g377,g380)
    c: Coincident(g379,g380)
    c: Equal(g6,g380)
    c: Parallel(g380,g6)
    c: Diameter(g381) = 6.35
    c: Coincident(g379,g382)
    c: Coincident(g381,g382)
    c: Equal(g6,g382)
    c: Parallel(g382,g6)
    c: Diameter(g383) = 6.35
    c: Coincident(g381,g384)
    c: Coincident(g383,g384)
    c: Equal(g6,g384)
    c: Parallel(g384,g6)
    c: Diameter(g385) = 6.35
    c: Coincident(g383,g386)
    c: Coincident(g385,g386)
    c: Equal(g6,g386)
    c: Parallel(g386,g6)
    c: Diameter(g387) = 6.35
    c: Coincident(g385,g388)
    c: Coincident(g387,g388)
    c: Equal(g6,g388)
    c: Parallel(g388,g6)
FEATURE [Part::Extrusion] Extrude
  Base = -> Sketch
  Dir = (0,0,1)
  DirMode = 2
  FaceMakerClass = Part::FaceMakerBullseye
  LengthFwd = 5.9944
  LengthRev = 0
  Solid = true
  Symmetric = false
FEATURE [TechDraw::DrawSVGTemplate] Template
  Height = 215.9
  Orientation = 1
  Width = 279.4
FEATURE [TechDraw::DrawProjGroupItem] ProjItem  label="Front"
  CoarseView = false
  Direction = (0,0,1)
  Focus = 100
  HardHidden = false
  IsoCount = 0
  IsoHidden = false
  IsoVisible = false
  LockPosition = true
  Perspective = false
  Rotation = 0
  RotationVector = (1,0,0)
  Scale = 0.2
  ScaleType = 2
  SeamHidden = false
  SeamVisible = true
  SmoothHidden = false
  SmoothVisible = true
  Source = -> [Extrude]
  Type = 0
  X = 0
  XDirection = (1,0,0)
  Y = 0
FEATURE [TechDraw::DrawProjGroupItem] ProjItem001  label="Left"
  CoarseView = false
  Direction = (-1,0,1e-16)
  Focus = 100
  HardHidden = false
  IsoCount = 0
  IsoHidden = false
  IsoVisible = false
  LockPosition = false
  Perspective = false
  Rotation = 0
  RotationVector = (1,0,0)
  Scale = 0.2
  ScaleType = 2
  SeamHidden = false
  SeamVisible = true
  SmoothHidden = false
  SmoothVisible = true
  Source = -> [Extrude]
  Type = 1
  X = 108.904
  XDirection = (1e-16,0,1)
  Y = 0
FEATURE [TechDraw::DrawProjGroup] ProjGroup
  Anchor = -> ProjItem
  AutoDistribute = true
  LockPosition = false
  ProjectionType = 0
  Rotation = 0
  Scale = 0.2
  ScaleType = 2
  Source = -> [Extrude]
  Views = -> [ProjItem,ProjItem001]
  X = 128.828
  Y = 99.3385
  spacingX = 15.0114
  spacingY = 15.0114
FEATURE [TechDraw::DrawViewDimension] Dimension
  Arbitrary = false
  ArbitraryTolerances = false
  EqualTolerance = true
  FormatSpec = %.3f
  FormatSpecOverTolerance = %+.3f
  FormatSpecUnderTolerance = %+.3f
  Inverted = false
  LockPosition = false
  MeasureType = 1
  OverTolerance = 0
  References2D = -> [ProjItem]
  Rotation = 0
  ScaleType = 0
  TheoreticalExact = false
  Type = 1
  UnderTolerance = 0
  X = -4.03785
  Y = -76.2238
FEATURE [TechDraw::DrawViewDimension] Dimension002
  Arbitrary = false
  ArbitraryTolerances = false
  EqualTolerance = true
  FormatSpec = %.3f
  FormatSpecOverTolerance = %+.3f
  FormatSpecUnderTolerance = %+.3f
  Inverted = false
  LockPosition = false
  MeasureType = 1
  OverTolerance = 0
  References2D = -> [ProjItem]
  Rotation = 0
  ScaleType = 0
  TheoreticalExact = false
  Type = 2
  UnderTolerance = 0
  X = 84.6611
  Y = 2.53687
FEATURE [TechDraw::DrawViewDimension] Dimension013
  Arbitrary = false
  ArbitraryTolerances = false
  EqualTolerance = true
  FormatSpec = %.3f
  FormatSpecOverTolerance = %+.3f
  FormatSpecUnderTolerance = %+.3f
  Inverted = false
  LockPosition = false
  MeasureType = 1
  OverTolerance = 0
  References2D = -> [ProjItem001]
  Rotation = 0
  ScaleType = 0
  TheoreticalExact = false
  Type = 1
  UnderTolerance = 0
  X = 14.1018
  Y = 67.5473
FEATURE [TechDraw::DrawViewAnnotation] Annotation
  Font = osifont
  LineSpace = 80
  LockPosition = false
  MaxWidth = -1
  Rotation = 0
  ScaleType = 0
  Text = Repeat with equal spacing
  TextSize = 5.0038
  TextStyle = 0
  X = 131.963
  Y = 158.523
FEATURE [TechDraw::DrawHatch] Hatch002  label="Hatch002F0"
  HatchPattern = <path>
  Source = -> ProjItem001 [Face0]
FEATURE [TechDraw::DrawHatch] Hatch  label="HatchF0"
  HatchPattern = <path>
  Source = -> ProjItem [Face0]
FEATURE [TechDraw::DrawViewAnnotation] Annotation001
  Font = osifont
  LineSpace = 80
  LockPosition = false
  MaxWidth = -1
  Rotation = 0
  ScaleType = 0
  Text = Figure S1 (Inverted 1) | Panel 1 [left side interior baffle] | Quantity: 1
  TextSize = 5.0038
  TextStyle = 0
  X = 45.5256
  Y = 195.58
FEATURE [TechDraw::DrawViewAnnotation] Annotation003
  Font = osifont
  LineSpace = 80
  LockPosition = false
  MaxWidth = -1
  Rotation = 0
  ScaleType = 0
  Text = Units: Inches
  TextSize = 5.0038
  TextStyle = 0
  X = 259.08
  Y = 5.08
FEATURE [TechDraw::DrawViewDimension] Dimension014
  Arbitrary = false
  ArbitraryTolerances = false
  EqualTolerance = true
  FormatSpec = ⌀%.3f
  FormatSpecOverTolerance = %+.3f
  FormatSpecUnderTolerance = %+.3f
  Inverted = false
  LockPosition = false
  MeasureType = 1
  OverTolerance = 0
  References2D = -> [ProjItem]
  Rotation = 0
  ScaleType = 0
  TheoreticalExact = false
  Type = 5
  UnderTolerance = 0
  X = -82.9563
  Y = 82.5704
FEATURE [TechDraw::DrawViewDimension] Dimension015
  Arbitrary = false
  ArbitraryTolerances = false
  EqualTolerance = true
  FormatSpec = %.3f
  FormatSpecOverTolerance = %+.3f
  FormatSpecUnderTolerance = %+.3f
  Inverted = false
  LockPosition = false
  MeasureType = 1
  OverTolerance = 0
  References2D = -> [ProjItem]
  Rotation = 0
  ScaleType = 0
  TheoreticalExact = false
  Type = 1
  UnderTolerance = 0
  X = -91.1739
  Y = 56.7292
FEATURE [TechDraw::DrawViewDimension] Dimension016
  Arbitrary = false
  ArbitraryTolerances = false
  EqualTolerance = true
  FormatSpec = %.3f
  FormatSpecOverTolerance = %+.3f
  FormatSpecUnderTolerance = %+.3f
  Inverted = false
  LockPosition = false
  MeasureType = 1
  OverTolerance = 0
  References2D = -> [ProjItem]
  Rotation = 0
  ScaleType = 0
  TheoreticalExact = false
  Type = 2
  UnderTolerance = 0
  X = -59.724
  Y = 84.5232
FEATURE [TechDraw::DrawViewDimension] Dimension017
  Arbitrary = false
  ArbitraryTolerances = false
  EqualTolerance = true
  FormatSpec = %.3f
  FormatSpecOverTolerance = %+.3f
  FormatSpecUnderTolerance = %+.3f
  Inverted = false
  LockPosition = false
  MeasureType = 1
  OverTolerance = 0
  References2D = -> [ProjItem]
  Rotation = 0
  ScaleType = 0
  TheoreticalExact = false
  Type = 1
  UnderTolerance = 0
  X = -46.7031
  Y = 33.4292
FEATURE [TechDraw::DrawViewDimension] Dimension018
  Arbitrary = false
  ArbitraryTolerances = false
  EqualTolerance = true
  FormatSpec = %.3f
  FormatSpecOverTolerance = %+.3f
  FormatSpecUnderTolerance = %+.3f
  Inverted = false
  LockPosition = false
  MeasureType = 1
  OverTolerance = 0
  References2D = -> [ProjItem]
  Rotation = 0
  ScaleType = 0
  TheoreticalExact = false
  Type = 2
  UnderTolerance = 0
  X = -34.0738
  Y = 41.3078
FEATURE [TechDraw::DrawPage] Page
  KeepUpdated = true
  NextBalloonIndex = 2
  ProjectionType = 0
  Template = -> Template
  Views = -> [ProjGroup,Dimension,Dimension002,Dimension013,Annotation,Annotation001,Annotation003,Dimension014,Dimension015,Dimension016,Dimension017,Dimension018]
note: 2 file-system paths scrubbed to <path> (originals preserved in the JSON sidecar)
